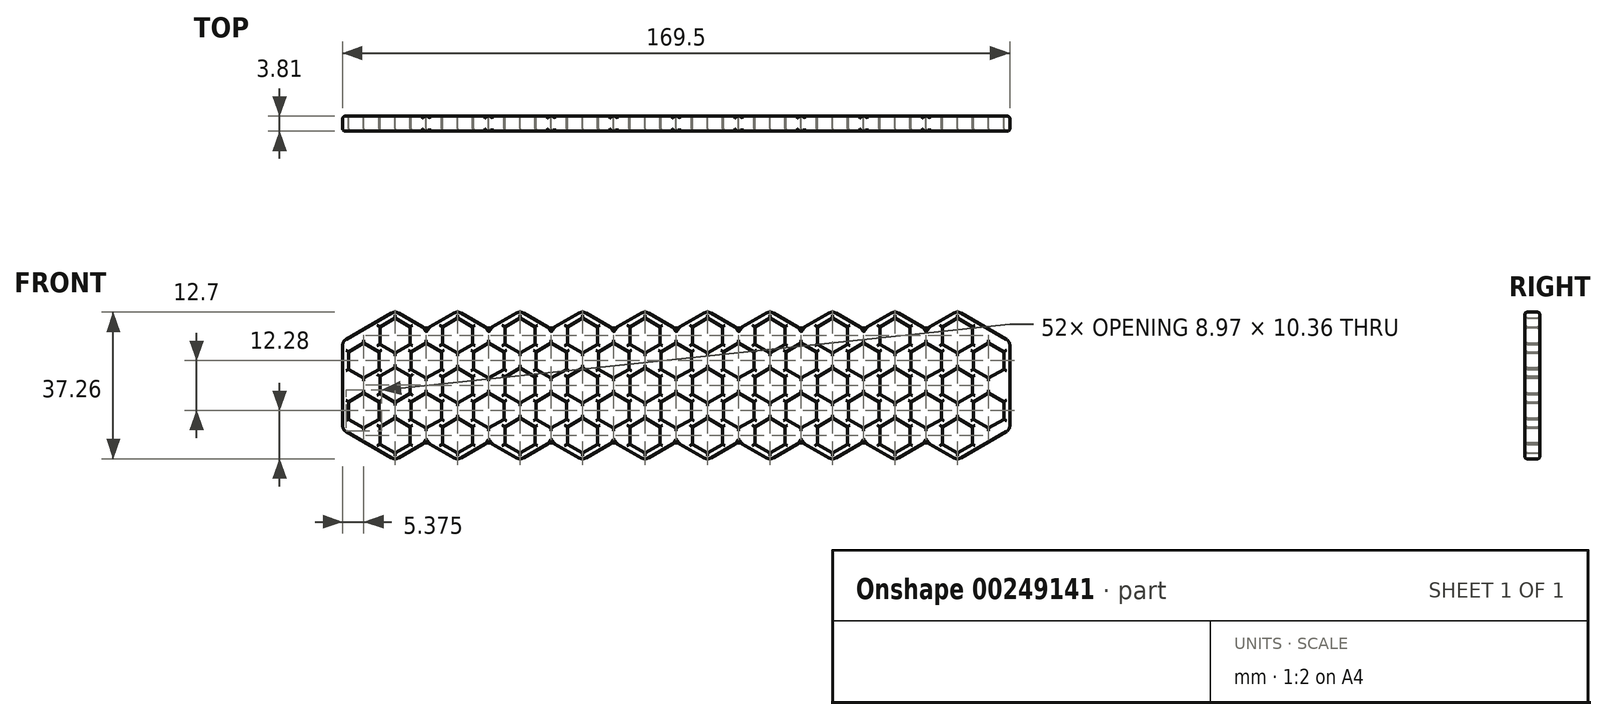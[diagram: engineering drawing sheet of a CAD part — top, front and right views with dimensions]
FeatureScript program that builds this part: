
annotation { "Feature Type Name" : "Feature", "Feature Type Description" : "" }
export const myFeature = defineFeature(function(context is Context, id is Id, definition is map)
    precondition{}
    {
        {
            var Q0;
            Q0=qCreatedBy(makeId("Front.planeOp"),FACE);
            var sketch = newSketch(context, id + "F3", { "sketchPlane" : qUnion([Q0])});
            skPoint(sketch, "E0.middle", {"position": v(0, 0) * mm});
            skPoint(sketch, "E1.cCircle.centerSnap0", {"position": v(-63.5, 0) * mm});
            skLineSegment(sketch, "E1.0", {"start": v(-63.5, 1.9) * mm, "end": v(-67.35, 4.13) * mm});
            skLineSegment(sketch, "E1.1", {"start": v(-67.35, 4.13) * mm, "end": v(-67.35, 8.57) * mm});
            skLineSegment(sketch, "E1.2", {"start": v(-67.35, 8.57) * mm, "end": v(-63.5, 10.8) * mm});
            skLineSegment(sketch, "E1.3", {"start": v(-63.5, 10.8) * mm, "end": v(-59.65, 8.57) * mm});
            skLineSegment(sketch, "E1.4", {"start": v(-59.65, 8.57) * mm, "end": v(-59.65, 4.13) * mm});
            skLineSegment(sketch, "E1.5", {"start": v(-59.65, 4.13) * mm, "end": v(-63.5, 1.9) * mm});
            skLineSegment(sketch, "E2.0", {"start": v(-71.45, -4.29) * mm, "end": v(-75.3, -2.06) * mm});
            skLineSegment(sketch, "E2.1", {"start": v(-75.3, -2.06) * mm, "end": v(-75.3, 2.38) * mm});
            skLineSegment(sketch, "E2.2", {"start": v(-75.3, 2.38) * mm, "end": v(-71.45, 4.6) * mm});
            skLineSegment(sketch, "E2.3", {"start": v(-71.45, 4.6) * mm, "end": v(-67.6, 2.38) * mm});
            skLineSegment(sketch, "E2.4", {"start": v(-67.6, 2.38) * mm, "end": v(-67.6, -2.06) * mm});
            skLineSegment(sketch, "E2.5", {"start": v(-67.6, -2.06) * mm, "end": v(-71.45, -4.29) * mm});
            skLineSegment(sketch, "E3.0", {"start": v(-63.5, -10.8) * mm, "end": v(-67.35, -8.57) * mm});
            skLineSegment(sketch, "E3.1", {"start": v(-67.35, -8.57) * mm, "end": v(-67.35, -4.13) * mm});
            skLineSegment(sketch, "E3.2", {"start": v(-67.35, -4.13) * mm, "end": v(-63.5, -1.9) * mm});
            skLineSegment(sketch, "E3.3", {"start": v(-63.5, -1.9) * mm, "end": v(-59.65, -4.13) * mm});
            skLineSegment(sketch, "E3.4", {"start": v(-59.65, -4.13) * mm, "end": v(-59.65, -8.57) * mm});
            skLineSegment(sketch, "E3.5", {"start": v(-59.65, -8.57) * mm, "end": v(-63.5, -10.8) * mm});
            skLineSegment(sketch, "E4.0", {"start": v(-47.63, 1.9) * mm, "end": v(-51.47, 4.13) * mm});
            skLineSegment(sketch, "E4.1", {"start": v(-51.47, 4.13) * mm, "end": v(-51.47, 8.57) * mm});
            skLineSegment(sketch, "E4.2", {"start": v(-51.47, 8.57) * mm, "end": v(-47.63, 10.8) * mm});
            skLineSegment(sketch, "E4.3", {"start": v(-47.63, 10.8) * mm, "end": v(-43.78, 8.57) * mm});
            skLineSegment(sketch, "E4.4", {"start": v(-43.78, 8.57) * mm, "end": v(-43.78, 4.13) * mm});
            skLineSegment(sketch, "E4.5", {"start": v(-43.78, 4.13) * mm, "end": v(-47.63, 1.9) * mm});
            skLineSegment(sketch, "E5.0", {"start": v(-47.63, -10.8) * mm, "end": v(-51.47, -8.57) * mm});
            skLineSegment(sketch, "E5.1", {"start": v(-51.47, -8.57) * mm, "end": v(-51.47, -4.13) * mm});
            skLineSegment(sketch, "E5.2", {"start": v(-51.47, -4.13) * mm, "end": v(-47.27, -1.7) * mm});
            skLineSegment(sketch, "E5.3", {"start": v(-47.63, -1.9) * mm, "end": v(-43.78, -4.13) * mm});
            skLineSegment(sketch, "E5.4", {"start": v(-43.78, -4.13) * mm, "end": v(-43.78, -8.57) * mm});
            skLineSegment(sketch, "E5.5", {"start": v(-43.78, -8.57) * mm, "end": v(-47.63, -10.8) * mm});
            skLineSegment(sketch, "E6.0", {"start": v(-31.75, 10.8) * mm, "end": v(-27.9, 8.57) * mm});
            skLineSegment(sketch, "E6.1", {"start": v(-27.9, 8.57) * mm, "end": v(-27.9, 4.13) * mm});
            skLineSegment(sketch, "E6.2", {"start": v(-27.9, 4.13) * mm, "end": v(-31.75, 1.9) * mm});
            skLineSegment(sketch, "E6.3", {"start": v(-31.75, 1.9) * mm, "end": v(-35.6, 4.13) * mm});
            skLineSegment(sketch, "E6.4", {"start": v(-35.6, 4.13) * mm, "end": v(-35.6, 8.57) * mm});
            skLineSegment(sketch, "E6.5", {"start": v(-35.6, 8.57) * mm, "end": v(-31.75, 10.8) * mm});
            skLineSegment(sketch, "E7.0", {"start": v(-31.75, -10.8) * mm, "end": v(-35.6, -8.57) * mm});
            skLineSegment(sketch, "E7.1", {"start": v(-35.6, -8.57) * mm, "end": v(-35.6, -4.13) * mm});
            skLineSegment(sketch, "E7.2", {"start": v(-35.6, -4.13) * mm, "end": v(-31.75, -1.9) * mm});
            skLineSegment(sketch, "E7.3", {"start": v(-31.75, -1.9) * mm, "end": v(-27.9, -4.13) * mm});
            skLineSegment(sketch, "E7.4", {"start": v(-27.9, -4.13) * mm, "end": v(-27.9, -8.57) * mm});
            skLineSegment(sketch, "E7.5", {"start": v(-27.9, -8.57) * mm, "end": v(-31.75, -10.8) * mm});
            skLineSegment(sketch, "E8.0", {"start": v(-15.88, 10.8) * mm, "end": v(-12.03, 8.57) * mm});
            skLineSegment(sketch, "E8.1", {"start": v(-12.03, 8.57) * mm, "end": v(-12.03, 4.13) * mm});
            skLineSegment(sketch, "E8.2", {"start": v(-12.03, 4.13) * mm, "end": v(-15.88, 1.9) * mm});
            skLineSegment(sketch, "E8.3", {"start": v(-15.88, 1.9) * mm, "end": v(-19.72, 4.13) * mm});
            skLineSegment(sketch, "E8.4", {"start": v(-19.72, 4.13) * mm, "end": v(-19.72, 8.57) * mm});
            skLineSegment(sketch, "E8.5", {"start": v(-19.72, 8.57) * mm, "end": v(-15.88, 10.8) * mm});
            skLineSegment(sketch, "E9.0", {"start": v(-15.88, -10.8) * mm, "end": v(-19.72, -8.57) * mm});
            skLineSegment(sketch, "E9.1", {"start": v(-19.72, -8.57) * mm, "end": v(-19.72, -4.13) * mm});
            skLineSegment(sketch, "E9.2", {"start": v(-19.72, -4.13) * mm, "end": v(-15.88, -1.9) * mm});
            skLineSegment(sketch, "E9.3", {"start": v(-15.88, -1.9) * mm, "end": v(-12.03, -4.13) * mm});
            skLineSegment(sketch, "E9.4", {"start": v(-12.03, -4.13) * mm, "end": v(-12.03, -8.57) * mm});
            skLineSegment(sketch, "E9.5", {"start": v(-12.03, -8.57) * mm, "end": v(-15.88, -10.8) * mm});
            skLineSegment(sketch, "E10.0", {"start": v(0, 10.8) * mm, "end": v(3.85, 8.57) * mm});
            skLineSegment(sketch, "E10.1", {"start": v(3.85, 8.57) * mm, "end": v(3.85, 4.13) * mm});
            skLineSegment(sketch, "E10.2", {"start": v(3.85, 4.13) * mm, "end": v(0, 1.9) * mm});
            skLineSegment(sketch, "E10.3", {"start": v(0, 1.9) * mm, "end": v(-3.85, 4.13) * mm});
            skLineSegment(sketch, "E10.4", {"start": v(-3.85, 4.13) * mm, "end": v(-3.85, 8.57) * mm});
            skLineSegment(sketch, "E10.5", {"start": v(-3.85, 8.57) * mm, "end": v(0, 10.8) * mm});
            skLineSegment(sketch, "E11.0", {"start": v(0, -10.8) * mm, "end": v(-3.85, -8.57) * mm});
            skLineSegment(sketch, "E11.1", {"start": v(-3.85, -8.57) * mm, "end": v(-3.85, -4.13) * mm});
            skLineSegment(sketch, "E11.2", {"start": v(-3.85, -4.13) * mm, "end": v(0, -1.9) * mm});
            skLineSegment(sketch, "E11.3", {"start": v(0, -1.9) * mm, "end": v(3.85, -4.13) * mm});
            skLineSegment(sketch, "E11.4", {"start": v(3.85, -4.13) * mm, "end": v(3.85, -8.57) * mm});
            skLineSegment(sketch, "E11.5", {"start": v(3.85, -8.57) * mm, "end": v(0, -10.8) * mm});
            skLineSegment(sketch, "E12.0", {"start": v(15.87, 10.8) * mm, "end": v(19.72, 8.57) * mm});
            skLineSegment(sketch, "E12.1", {"start": v(19.72, 8.57) * mm, "end": v(19.72, 4.13) * mm});
            skLineSegment(sketch, "E12.2", {"start": v(19.72, 4.13) * mm, "end": v(15.87, 1.9) * mm});
            skLineSegment(sketch, "E12.3", {"start": v(15.87, 1.9) * mm, "end": v(12.03, 4.13) * mm});
            skLineSegment(sketch, "E12.4", {"start": v(12.03, 4.13) * mm, "end": v(12.03, 8.57) * mm});
            skLineSegment(sketch, "E12.5", {"start": v(12.03, 8.57) * mm, "end": v(15.87, 10.8) * mm});
            skLineSegment(sketch, "E13.0", {"start": v(15.87, -10.8) * mm, "end": v(12.03, -8.57) * mm});
            skLineSegment(sketch, "E13.1", {"start": v(12.03, -8.57) * mm, "end": v(12.03, -4.13) * mm});
            skLineSegment(sketch, "E13.2", {"start": v(12.03, -4.13) * mm, "end": v(15.87, -1.9) * mm});
            skLineSegment(sketch, "E13.3", {"start": v(15.87, -1.9) * mm, "end": v(19.72, -4.13) * mm});
            skLineSegment(sketch, "E13.4", {"start": v(19.72, -4.13) * mm, "end": v(19.72, -8.57) * mm});
            skLineSegment(sketch, "E13.5", {"start": v(19.72, -8.57) * mm, "end": v(15.87, -10.8) * mm});
            skPoint(sketch, "E14.cCircle.perimeterSnap0", {"position": v(31.75, 0) * mm});
            skLineSegment(sketch, "E14.0", {"start": v(31.75, 10.8) * mm, "end": v(35.6, 8.57) * mm});
            skPoint(sketch, "E14.0.startSnap0", {"position": v(31.75, 0) * mm});
            skLineSegment(sketch, "E14.1", {"start": v(35.6, 8.57) * mm, "end": v(35.6, 4.13) * mm});
            skLineSegment(sketch, "E14.2", {"start": v(35.6, 4.13) * mm, "end": v(31.75, 1.9) * mm});
            skLineSegment(sketch, "E14.3", {"start": v(31.75, 1.9) * mm, "end": v(27.9, 4.13) * mm});
            skLineSegment(sketch, "E14.4", {"start": v(27.9, 4.13) * mm, "end": v(27.9, 8.57) * mm});
            skLineSegment(sketch, "E14.5", {"start": v(27.9, 8.57) * mm, "end": v(31.75, 10.8) * mm});
            skLineSegment(sketch, "E15.0", {"start": v(31.75, -10.8) * mm, "end": v(27.9, -8.57) * mm});
            skLineSegment(sketch, "E15.1", {"start": v(27.9, -8.57) * mm, "end": v(27.9, -4.13) * mm});
            skLineSegment(sketch, "E15.2", {"start": v(27.9, -4.13) * mm, "end": v(31.75, -1.9) * mm});
            skLineSegment(sketch, "E15.3", {"start": v(31.75, -1.9) * mm, "end": v(35.6, -4.13) * mm});
            skLineSegment(sketch, "E15.4", {"start": v(35.6, -4.13) * mm, "end": v(35.6, -8.57) * mm});
            skLineSegment(sketch, "E15.5", {"start": v(35.6, -8.57) * mm, "end": v(31.75, -10.8) * mm});
            skLineSegment(sketch, "E16.0", {"start": v(47.62, 10.8) * mm, "end": v(51.47, 8.57) * mm});
            skLineSegment(sketch, "E16.1", {"start": v(51.47, 8.57) * mm, "end": v(51.47, 4.13) * mm});
            skLineSegment(sketch, "E16.2", {"start": v(51.47, 4.13) * mm, "end": v(47.62, 1.9) * mm});
            skLineSegment(sketch, "E16.3", {"start": v(47.62, 1.9) * mm, "end": v(43.78, 4.13) * mm});
            skLineSegment(sketch, "E16.4", {"start": v(43.78, 4.13) * mm, "end": v(43.78, 8.57) * mm});
            skLineSegment(sketch, "E16.5", {"start": v(43.78, 8.57) * mm, "end": v(47.62, 10.8) * mm});
            skLineSegment(sketch, "E17.0", {"start": v(47.62, -10.8) * mm, "end": v(43.78, -8.57) * mm});
            skLineSegment(sketch, "E17.1", {"start": v(43.78, -8.57) * mm, "end": v(43.78, -4.13) * mm});
            skLineSegment(sketch, "E17.2", {"start": v(43.78, -4.13) * mm, "end": v(47.62, -1.9) * mm});
            skLineSegment(sketch, "E17.3", {"start": v(47.62, -1.9) * mm, "end": v(51.47, -4.13) * mm});
            skLineSegment(sketch, "E17.4", {"start": v(51.47, -4.13) * mm, "end": v(51.47, -8.57) * mm});
            skLineSegment(sketch, "E17.5", {"start": v(51.47, -8.57) * mm, "end": v(47.62, -10.8) * mm});
            skLineSegment(sketch, "E18.0", {"start": v(63.5, 10.8) * mm, "end": v(67.35, 8.57) * mm});
            skLineSegment(sketch, "E18.1", {"start": v(67.35, 8.57) * mm, "end": v(67.35, 4.13) * mm});
            skLineSegment(sketch, "E18.2", {"start": v(67.35, 4.13) * mm, "end": v(63.5, 1.9) * mm});
            skLineSegment(sketch, "E18.3", {"start": v(63.5, 1.9) * mm, "end": v(59.65, 4.13) * mm});
            skLineSegment(sketch, "E18.4", {"start": v(59.65, 4.13) * mm, "end": v(59.65, 8.57) * mm});
            skLineSegment(sketch, "E18.5", {"start": v(59.65, 8.57) * mm, "end": v(63.5, 10.8) * mm});
            skLineSegment(sketch, "E19.0", {"start": v(63.5, -10.8) * mm, "end": v(59.65, -8.57) * mm});
            skLineSegment(sketch, "E19.1", {"start": v(59.65, -8.57) * mm, "end": v(59.65, -4.13) * mm});
            skLineSegment(sketch, "E19.2", {"start": v(59.65, -4.13) * mm, "end": v(63.5, -1.9) * mm});
            skLineSegment(sketch, "E19.3", {"start": v(63.5, -1.9) * mm, "end": v(67.35, -4.13) * mm});
            skLineSegment(sketch, "E19.4", {"start": v(67.35, -4.13) * mm, "end": v(67.35, -8.57) * mm});
            skLineSegment(sketch, "E19.5", {"start": v(67.35, -8.57) * mm, "end": v(63.5, -10.8) * mm});
            skPoint(sketch, "E20.cCircle.centerSnap0", {"position": v(-55.58, 0.35) * mm});
            skLineSegment(sketch, "E20.0", {"start": v(-55.58, -4.44) * mm, "end": v(-59.42, -2.22) * mm});
            skLineSegment(sketch, "E20.1", {"start": v(-59.42, -2.22) * mm, "end": v(-59.42, 2.22) * mm});
            skLineSegment(sketch, "E20.2", {"start": v(-59.42, 2.22) * mm, "end": v(-55.58, 4.44) * mm});
            skLineSegment(sketch, "E20.3", {"start": v(-55.58, 4.44) * mm, "end": v(-51.73, 2.22) * mm});
            skLineSegment(sketch, "E20.4", {"start": v(-51.73, 2.22) * mm, "end": v(-51.73, -2.22) * mm});
            skLineSegment(sketch, "E20.5", {"start": v(-51.73, -2.22) * mm, "end": v(-55.58, -4.44) * mm});
            skLineSegment(sketch, "E21.0", {"start": v(-39.7, -4.44) * mm, "end": v(-43.55, -2.22) * mm});
            skLineSegment(sketch, "E21.1", {"start": v(-43.55, -2.22) * mm, "end": v(-43.55, 2.22) * mm});
            skLineSegment(sketch, "E21.2", {"start": v(-43.55, 2.22) * mm, "end": v(-39.7, 4.44) * mm});
            skLineSegment(sketch, "E21.3", {"start": v(-39.7, 4.44) * mm, "end": v(-35.85, 2.22) * mm});
            skLineSegment(sketch, "E21.4", {"start": v(-35.85, 2.22) * mm, "end": v(-35.85, -2.22) * mm});
            skLineSegment(sketch, "E21.5", {"start": v(-35.85, -2.22) * mm, "end": v(-39.7, -4.44) * mm});
            skPoint(sketch, "E22.cCircle.centerSnap0", {"position": v(-23.83, 0.35) * mm});
            skLineSegment(sketch, "E22.0", {"start": v(-23.83, 4.45) * mm, "end": v(-19.98, 2.22) * mm});
            skLineSegment(sketch, "E22.1", {"start": v(-19.98, 2.22) * mm, "end": v(-19.98, -2.22) * mm});
            skLineSegment(sketch, "E22.2", {"start": v(-19.98, -2.22) * mm, "end": v(-23.83, -4.44) * mm});
            skLineSegment(sketch, "E22.3", {"start": v(-23.83, -4.44) * mm, "end": v(-27.67, -2.22) * mm});
            skLineSegment(sketch, "E22.4", {"start": v(-27.67, -2.22) * mm, "end": v(-27.67, 2.22) * mm});
            skLineSegment(sketch, "E22.5", {"start": v(-27.67, 2.22) * mm, "end": v(-23.83, 4.45) * mm});
            skPoint(sketch, "E23.cCircle.centerSnap0", {"position": v(-7.95, 0.35) * mm});
            skLineSegment(sketch, "E23.0", {"start": v(-7.95, -4.44) * mm, "end": v(-11.8, -2.22) * mm});
            skLineSegment(sketch, "E23.1", {"start": v(-11.8, -2.22) * mm, "end": v(-11.8, 2.22) * mm});
            skLineSegment(sketch, "E23.2", {"start": v(-11.8, 2.22) * mm, "end": v(-7.95, 4.45) * mm});
            skLineSegment(sketch, "E23.3", {"start": v(-7.95, 4.45) * mm, "end": v(-4.1, 2.22) * mm});
            skLineSegment(sketch, "E23.4", {"start": v(-4.1, 2.22) * mm, "end": v(-4.1, -2.22) * mm});
            skLineSegment(sketch, "E23.5", {"start": v(-4.1, -2.22) * mm, "end": v(-7.95, -4.44) * mm});
            skPoint(sketch, "E24.cCircle.centerSnap0", {"position": v(7.92, 0.35) * mm});
            skLineSegment(sketch, "E24.0", {"start": v(7.92, -4.44) * mm, "end": v(4.08, -2.22) * mm});
            skLineSegment(sketch, "E24.1", {"start": v(4.08, -2.22) * mm, "end": v(4.08, 2.22) * mm});
            skLineSegment(sketch, "E24.2", {"start": v(4.08, 2.22) * mm, "end": v(7.92, 4.45) * mm});
            skLineSegment(sketch, "E24.3", {"start": v(7.92, 4.45) * mm, "end": v(11.77, 2.22) * mm});
            skLineSegment(sketch, "E24.4", {"start": v(11.77, 2.22) * mm, "end": v(11.77, -2.22) * mm});
            skLineSegment(sketch, "E24.5", {"start": v(11.77, -2.22) * mm, "end": v(7.92, -4.44) * mm});
            skPoint(sketch, "E25.cCircle.centerSnap0", {"position": v(23.8, 0.35) * mm});
            skLineSegment(sketch, "E25.0", {"start": v(23.8, -4.44) * mm, "end": v(19.95, -2.22) * mm});
            skLineSegment(sketch, "E25.1", {"start": v(19.95, -2.22) * mm, "end": v(19.95, 2.22) * mm});
            skLineSegment(sketch, "E25.2", {"start": v(19.95, 2.22) * mm, "end": v(23.8, 4.45) * mm});
            skLineSegment(sketch, "E25.3", {"start": v(23.8, 4.45) * mm, "end": v(27.65, 2.22) * mm});
            skLineSegment(sketch, "E25.4", {"start": v(27.65, 2.22) * mm, "end": v(27.65, -2.22) * mm});
            skLineSegment(sketch, "E25.5", {"start": v(27.65, -2.22) * mm, "end": v(23.8, -4.44) * mm});
            skLineSegment(sketch, "E26.0", {"start": v(39.67, 4.45) * mm, "end": v(43.52, 2.22) * mm});
            skLineSegment(sketch, "E26.1", {"start": v(43.52, 2.22) * mm, "end": v(43.52, -2.22) * mm});
            skLineSegment(sketch, "E26.2", {"start": v(43.52, -2.22) * mm, "end": v(39.67, -4.44) * mm});
            skLineSegment(sketch, "E26.3", {"start": v(39.67, -4.44) * mm, "end": v(35.83, -2.22) * mm});
            skLineSegment(sketch, "E26.4", {"start": v(35.83, -2.22) * mm, "end": v(35.83, 2.22) * mm});
            skLineSegment(sketch, "E26.5", {"start": v(35.83, 2.22) * mm, "end": v(39.67, 4.45) * mm});
            skLineSegment(sketch, "E27.0", {"start": v(55.55, -4.44) * mm, "end": v(51.7, -2.22) * mm});
            skLineSegment(sketch, "E27.1", {"start": v(51.7, -2.22) * mm, "end": v(51.7, 2.22) * mm});
            skLineSegment(sketch, "E27.2", {"start": v(51.7, 2.22) * mm, "end": v(55.55, 4.44) * mm});
            skLineSegment(sketch, "E27.3", {"start": v(55.55, 4.44) * mm, "end": v(59.4, 2.22) * mm});
            skLineSegment(sketch, "E27.4", {"start": v(59.4, 2.22) * mm, "end": v(59.4, -2.22) * mm});
            skLineSegment(sketch, "E27.5", {"start": v(59.4, -2.22) * mm, "end": v(55.55, -4.44) * mm});
            skLineSegment(sketch, "E28.0", {"start": v(71.42, -4.44) * mm, "end": v(67.58, -2.22) * mm});
            skLineSegment(sketch, "E28.1", {"start": v(67.58, -2.22) * mm, "end": v(67.58, 2.22) * mm});
            skLineSegment(sketch, "E28.2", {"start": v(67.58, 2.22) * mm, "end": v(71.42, 4.45) * mm});
            skLineSegment(sketch, "E28.3", {"start": v(71.42, 4.45) * mm, "end": v(75.27, 2.22) * mm});
            skLineSegment(sketch, "E28.4", {"start": v(75.27, 2.22) * mm, "end": v(75.27, -2.22) * mm});
            skLineSegment(sketch, "E28.5", {"start": v(75.27, -2.22) * mm, "end": v(71.42, -4.44) * mm});
            skLineSegment(sketch, "E29.0", {"start": v(-79.38, 1.9) * mm, "end": v(-83.22, 4.13) * mm});
            skLineSegment(sketch, "E29.1", {"start": v(-83.22, 4.13) * mm, "end": v(-83.22, 8.57) * mm});
            skLineSegment(sketch, "E29.2", {"start": v(-83.22, 8.57) * mm, "end": v(-79.38, 10.8) * mm});
            skLineSegment(sketch, "E29.3", {"start": v(-79.38, 10.8) * mm, "end": v(-75.53, 8.57) * mm});
            skLineSegment(sketch, "E29.4", {"start": v(-75.53, 8.57) * mm, "end": v(-75.53, 4.13) * mm});
            skLineSegment(sketch, "E29.5", {"start": v(-75.53, 4.13) * mm, "end": v(-79.38, 1.9) * mm});
            skLineSegment(sketch, "E30.0", {"start": v(-79.38, -10.8) * mm, "end": v(-83.22, -8.57) * mm});
            skLineSegment(sketch, "E30.1", {"start": v(-83.22, -8.57) * mm, "end": v(-83.22, -4.13) * mm});
            skLineSegment(sketch, "E30.2", {"start": v(-83.22, -4.13) * mm, "end": v(-79.38, -1.9) * mm});
            skLineSegment(sketch, "E30.3", {"start": v(-79.38, -1.9) * mm, "end": v(-75.53, -4.13) * mm});
            skLineSegment(sketch, "E30.4", {"start": v(-75.53, -4.13) * mm, "end": v(-75.53, -8.57) * mm});
            skLineSegment(sketch, "E30.5", {"start": v(-75.53, -8.57) * mm, "end": v(-79.38, -10.8) * mm});
            skPoint(sketch, "E31.orphan", {"position": v(-71.45, 13.02) * mm});
            skLineSegment(sketch, "E32.0", {"start": v(-71.45, 17.14) * mm, "end": v(-67.6, 14.92) * mm});
            skLineSegment(sketch, "E32.1", {"start": v(-67.6, 14.92) * mm, "end": v(-67.6, 10.48) * mm});
            skLineSegment(sketch, "E32.2", {"start": v(-67.6, 10.48) * mm, "end": v(-71.45, 8.26) * mm});
            skLineSegment(sketch, "E32.3", {"start": v(-71.45, 8.26) * mm, "end": v(-75.3, 10.48) * mm});
            skLineSegment(sketch, "E32.4", {"start": v(-75.3, 10.48) * mm, "end": v(-75.3, 14.92) * mm});
            skLineSegment(sketch, "E32.5", {"start": v(-75.3, 14.92) * mm, "end": v(-71.45, 17.15) * mm});
            skLineSegment(sketch, "E33.0", {"start": v(-55.58, 17.14) * mm, "end": v(-51.73, 14.92) * mm});
            skLineSegment(sketch, "E33.1", {"start": v(-51.73, 14.92) * mm, "end": v(-51.73, 10.48) * mm});
            skLineSegment(sketch, "E33.2", {"start": v(-51.73, 10.48) * mm, "end": v(-55.58, 8.26) * mm});
            skLineSegment(sketch, "E33.3", {"start": v(-55.58, 8.26) * mm, "end": v(-59.42, 10.48) * mm});
            skLineSegment(sketch, "E33.4", {"start": v(-59.42, 10.48) * mm, "end": v(-59.42, 14.92) * mm});
            skLineSegment(sketch, "E33.5", {"start": v(-59.42, 14.92) * mm, "end": v(-55.58, 17.15) * mm});
            skLineSegment(sketch, "E34.0", {"start": v(-39.7, 17.14) * mm, "end": v(-35.85, 14.92) * mm});
            skLineSegment(sketch, "E34.1", {"start": v(-35.85, 14.92) * mm, "end": v(-35.85, 10.48) * mm});
            skLineSegment(sketch, "E34.2", {"start": v(-35.85, 10.48) * mm, "end": v(-39.7, 8.26) * mm});
            skLineSegment(sketch, "E34.3", {"start": v(-39.7, 8.26) * mm, "end": v(-43.55, 10.48) * mm});
            skLineSegment(sketch, "E34.4", {"start": v(-43.55, 10.48) * mm, "end": v(-43.55, 14.92) * mm});
            skLineSegment(sketch, "E34.5", {"start": v(-43.55, 14.92) * mm, "end": v(-39.7, 17.14) * mm});
            skLineSegment(sketch, "E35.0", {"start": v(-23.83, 17.14) * mm, "end": v(-19.98, 14.92) * mm});
            skLineSegment(sketch, "E35.1", {"start": v(-19.98, 14.92) * mm, "end": v(-19.98, 10.48) * mm});
            skLineSegment(sketch, "E35.2", {"start": v(-19.98, 10.48) * mm, "end": v(-23.83, 8.26) * mm});
            skLineSegment(sketch, "E35.3", {"start": v(-23.83, 8.26) * mm, "end": v(-27.67, 10.48) * mm});
            skLineSegment(sketch, "E35.4", {"start": v(-27.67, 10.48) * mm, "end": v(-27.67, 14.92) * mm});
            skLineSegment(sketch, "E35.5", {"start": v(-27.67, 14.92) * mm, "end": v(-23.83, 17.15) * mm});
            skLineSegment(sketch, "E36.0", {"start": v(-7.95, 17.15) * mm, "end": v(-4.1, 14.92) * mm});
            skLineSegment(sketch, "E36.1", {"start": v(-4.1, 14.92) * mm, "end": v(-4.1, 10.48) * mm});
            skLineSegment(sketch, "E36.2", {"start": v(-4.1, 10.48) * mm, "end": v(-7.95, 8.26) * mm});
            skLineSegment(sketch, "E36.3", {"start": v(-7.95, 8.26) * mm, "end": v(-11.8, 10.48) * mm});
            skLineSegment(sketch, "E36.4", {"start": v(-11.8, 10.48) * mm, "end": v(-11.8, 14.92) * mm});
            skLineSegment(sketch, "E36.5", {"start": v(-11.8, 14.92) * mm, "end": v(-7.95, 17.15) * mm});
            skLineSegment(sketch, "E37.0", {"start": v(7.92, 17.15) * mm, "end": v(11.77, 14.92) * mm});
            skLineSegment(sketch, "E37.1", {"start": v(11.77, 14.92) * mm, "end": v(11.77, 10.48) * mm});
            skLineSegment(sketch, "E37.2", {"start": v(11.77, 10.48) * mm, "end": v(7.92, 8.26) * mm});
            skLineSegment(sketch, "E37.3", {"start": v(7.92, 8.26) * mm, "end": v(4.08, 10.48) * mm});
            skLineSegment(sketch, "E37.4", {"start": v(4.08, 10.48) * mm, "end": v(4.08, 14.92) * mm});
            skLineSegment(sketch, "E37.5", {"start": v(4.08, 14.92) * mm, "end": v(7.92, 17.15) * mm});
            skLineSegment(sketch, "E38.0", {"start": v(23.8, 17.15) * mm, "end": v(27.65, 14.92) * mm});
            skLineSegment(sketch, "E38.1", {"start": v(27.65, 14.92) * mm, "end": v(27.65, 10.48) * mm});
            skLineSegment(sketch, "E38.2", {"start": v(27.65, 10.48) * mm, "end": v(23.8, 8.26) * mm});
            skLineSegment(sketch, "E38.3", {"start": v(23.8, 8.26) * mm, "end": v(19.95, 10.48) * mm});
            skLineSegment(sketch, "E38.4", {"start": v(19.95, 10.48) * mm, "end": v(19.95, 14.92) * mm});
            skLineSegment(sketch, "E38.5", {"start": v(19.95, 14.92) * mm, "end": v(23.8, 17.15) * mm});
            skLineSegment(sketch, "E39.0", {"start": v(55.55, 17.15) * mm, "end": v(59.4, 14.92) * mm});
            skLineSegment(sketch, "E39.1", {"start": v(59.4, 14.92) * mm, "end": v(59.4, 10.48) * mm});
            skLineSegment(sketch, "E39.2", {"start": v(59.4, 10.48) * mm, "end": v(55.55, 8.26) * mm});
            skLineSegment(sketch, "E39.3", {"start": v(55.55, 8.26) * mm, "end": v(51.7, 10.48) * mm});
            skLineSegment(sketch, "E39.4", {"start": v(51.7, 10.48) * mm, "end": v(51.7, 14.92) * mm});
            skLineSegment(sketch, "E39.5", {"start": v(51.7, 14.92) * mm, "end": v(55.55, 17.15) * mm});
            skLineSegment(sketch, "E40.0", {"start": v(71.42, 17.15) * mm, "end": v(75.27, 14.92) * mm});
            skLineSegment(sketch, "E40.1", {"start": v(75.27, 14.92) * mm, "end": v(75.27, 10.48) * mm});
            skLineSegment(sketch, "E40.2", {"start": v(75.27, 10.48) * mm, "end": v(71.42, 8.25) * mm});
            skLineSegment(sketch, "E40.3", {"start": v(71.42, 8.25) * mm, "end": v(67.58, 10.48) * mm});
            skLineSegment(sketch, "E40.4", {"start": v(67.58, 10.48) * mm, "end": v(67.58, 14.92) * mm});
            skLineSegment(sketch, "E40.5", {"start": v(67.58, 14.92) * mm, "end": v(71.42, 17.15) * mm});
            skLineSegment(sketch, "E41.0", {"start": v(39.67, 17.15) * mm, "end": v(43.52, 14.92) * mm});
            skLineSegment(sketch, "E41.1", {"start": v(43.52, 14.92) * mm, "end": v(43.52, 10.48) * mm});
            skLineSegment(sketch, "E41.2", {"start": v(43.52, 10.48) * mm, "end": v(39.67, 8.26) * mm});
            skLineSegment(sketch, "E41.3", {"start": v(39.67, 8.26) * mm, "end": v(35.83, 10.48) * mm});
            skLineSegment(sketch, "E41.4", {"start": v(35.83, 10.48) * mm, "end": v(35.83, 14.92) * mm});
            skLineSegment(sketch, "E41.5", {"start": v(35.83, 14.92) * mm, "end": v(39.67, 17.15) * mm});
            skPoint(sketch, "E42.orphan", {"position": v(-55.58, -12) * mm});
            skPoint(sketch, "E43.orphan", {"position": v(-23.83, -12) * mm});
            skPoint(sketch, "E44.orphan", {"position": v(-7.95, -12) * mm});
            skPoint(sketch, "E45.orphan", {"position": v(7.92, -12) * mm});
            skPoint(sketch, "E46.orphan", {"position": v(23.8, -12) * mm});
            skLineSegment(sketch, "E47.0", {"start": v(-71.45, -17.14) * mm, "end": v(-75.3, -14.92) * mm});
            skLineSegment(sketch, "E47.1", {"start": v(-75.3, -14.92) * mm, "end": v(-75.3, -10.48) * mm});
            skLineSegment(sketch, "E47.2", {"start": v(-75.3, -10.48) * mm, "end": v(-71.45, -8.26) * mm});
            skLineSegment(sketch, "E47.3", {"start": v(-71.45, -8.26) * mm, "end": v(-67.6, -10.48) * mm});
            skLineSegment(sketch, "E47.4", {"start": v(-67.6, -10.48) * mm, "end": v(-67.6, -14.92) * mm});
            skLineSegment(sketch, "E47.5", {"start": v(-67.6, -14.92) * mm, "end": v(-71.45, -17.14) * mm});
            skLineSegment(sketch, "E48.0", {"start": v(-55.58, -17.14) * mm, "end": v(-59.42, -14.92) * mm});
            skLineSegment(sketch, "E48.1", {"start": v(-59.42, -14.92) * mm, "end": v(-59.42, -10.48) * mm});
            skLineSegment(sketch, "E48.2", {"start": v(-59.42, -10.48) * mm, "end": v(-55.58, -8.26) * mm});
            skLineSegment(sketch, "E48.3", {"start": v(-55.58, -8.26) * mm, "end": v(-51.73, -10.48) * mm});
            skLineSegment(sketch, "E48.4", {"start": v(-51.73, -10.48) * mm, "end": v(-51.73, -14.92) * mm});
            skLineSegment(sketch, "E48.5", {"start": v(-51.73, -14.92) * mm, "end": v(-55.58, -17.14) * mm});
            skLineSegment(sketch, "E49.0", {"start": v(-39.7, -17.14) * mm, "end": v(-43.55, -14.92) * mm});
            skLineSegment(sketch, "E49.1", {"start": v(-43.55, -14.92) * mm, "end": v(-43.55, -10.48) * mm});
            skLineSegment(sketch, "E49.2", {"start": v(-43.55, -10.48) * mm, "end": v(-39.7, -8.26) * mm});
            skLineSegment(sketch, "E49.3", {"start": v(-39.7, -8.26) * mm, "end": v(-35.85, -10.48) * mm});
            skLineSegment(sketch, "E49.4", {"start": v(-35.85, -10.48) * mm, "end": v(-35.85, -14.92) * mm});
            skLineSegment(sketch, "E49.5", {"start": v(-35.85, -14.92) * mm, "end": v(-39.7, -17.14) * mm});
            skLineSegment(sketch, "E50.0", {"start": v(-23.83, -17.14) * mm, "end": v(-27.67, -14.92) * mm});
            skLineSegment(sketch, "E50.1", {"start": v(-27.67, -14.92) * mm, "end": v(-27.67, -10.48) * mm});
            skLineSegment(sketch, "E50.2", {"start": v(-27.67, -10.48) * mm, "end": v(-23.83, -8.26) * mm});
            skLineSegment(sketch, "E50.3", {"start": v(-23.83, -8.26) * mm, "end": v(-19.98, -10.48) * mm});
            skLineSegment(sketch, "E50.4", {"start": v(-19.98, -10.48) * mm, "end": v(-19.98, -14.92) * mm});
            skLineSegment(sketch, "E50.5", {"start": v(-19.98, -14.92) * mm, "end": v(-23.83, -17.14) * mm});
            skLineSegment(sketch, "E51.0", {"start": v(-7.95, -17.14) * mm, "end": v(-11.8, -14.92) * mm});
            skLineSegment(sketch, "E51.1", {"start": v(-11.8, -14.92) * mm, "end": v(-11.8, -10.48) * mm});
            skLineSegment(sketch, "E51.2", {"start": v(-11.8, -10.48) * mm, "end": v(-7.95, -8.26) * mm});
            skLineSegment(sketch, "E51.3", {"start": v(-7.95, -8.26) * mm, "end": v(-4.1, -10.48) * mm});
            skLineSegment(sketch, "E51.4", {"start": v(-4.1, -10.48) * mm, "end": v(-4.1, -14.92) * mm});
            skLineSegment(sketch, "E51.5", {"start": v(-4.1, -14.92) * mm, "end": v(-7.95, -17.14) * mm});
            skLineSegment(sketch, "E52.0", {"start": v(7.92, -17.14) * mm, "end": v(4.08, -14.92) * mm});
            skLineSegment(sketch, "E52.1", {"start": v(4.08, -14.92) * mm, "end": v(4.08, -10.48) * mm});
            skLineSegment(sketch, "E52.2", {"start": v(4.08, -10.48) * mm, "end": v(7.92, -8.26) * mm});
            skLineSegment(sketch, "E52.3", {"start": v(7.92, -8.26) * mm, "end": v(11.77, -10.48) * mm});
            skLineSegment(sketch, "E52.4", {"start": v(11.77, -10.48) * mm, "end": v(11.77, -14.92) * mm});
            skLineSegment(sketch, "E52.5", {"start": v(11.77, -14.92) * mm, "end": v(7.92, -17.14) * mm});
            skLineSegment(sketch, "E53.0", {"start": v(23.8, -17.14) * mm, "end": v(19.95, -14.92) * mm});
            skLineSegment(sketch, "E53.1", {"start": v(19.95, -14.92) * mm, "end": v(19.95, -10.48) * mm});
            skLineSegment(sketch, "E53.2", {"start": v(19.95, -10.48) * mm, "end": v(23.8, -8.26) * mm});
            skLineSegment(sketch, "E53.3", {"start": v(23.8, -8.26) * mm, "end": v(27.65, -10.48) * mm});
            skLineSegment(sketch, "E53.4", {"start": v(27.65, -10.48) * mm, "end": v(27.65, -14.92) * mm});
            skLineSegment(sketch, "E53.5", {"start": v(27.65, -14.92) * mm, "end": v(23.8, -17.14) * mm});
            skLineSegment(sketch, "E54.0", {"start": v(39.67, -17.14) * mm, "end": v(35.83, -14.92) * mm});
            skLineSegment(sketch, "E54.1", {"start": v(35.83, -14.92) * mm, "end": v(35.83, -10.48) * mm});
            skLineSegment(sketch, "E54.2", {"start": v(35.83, -10.48) * mm, "end": v(39.67, -8.26) * mm});
            skLineSegment(sketch, "E54.3", {"start": v(39.67, -8.26) * mm, "end": v(43.52, -10.48) * mm});
            skLineSegment(sketch, "E54.4", {"start": v(43.52, -10.48) * mm, "end": v(43.52, -14.92) * mm});
            skLineSegment(sketch, "E54.5", {"start": v(43.52, -14.92) * mm, "end": v(39.67, -17.14) * mm});
            skLineSegment(sketch, "E55.0", {"start": v(55.55, -17.14) * mm, "end": v(51.7, -14.92) * mm});
            skLineSegment(sketch, "E55.1", {"start": v(51.7, -14.92) * mm, "end": v(51.7, -10.48) * mm});
            skLineSegment(sketch, "E55.2", {"start": v(51.7, -10.48) * mm, "end": v(55.55, -8.26) * mm});
            skLineSegment(sketch, "E55.3", {"start": v(55.55, -8.26) * mm, "end": v(59.4, -10.48) * mm});
            skLineSegment(sketch, "E55.4", {"start": v(59.4, -10.48) * mm, "end": v(59.4, -14.92) * mm});
            skLineSegment(sketch, "E55.5", {"start": v(59.4, -14.92) * mm, "end": v(55.55, -17.14) * mm});
            skLineSegment(sketch, "E56.0", {"start": v(71.42, -17.14) * mm, "end": v(67.58, -14.92) * mm});
            skLineSegment(sketch, "E56.1", {"start": v(67.58, -14.92) * mm, "end": v(67.58, -10.48) * mm});
            skLineSegment(sketch, "E56.2", {"start": v(67.58, -10.48) * mm, "end": v(71.42, -8.25) * mm});
            skLineSegment(sketch, "E56.3", {"start": v(71.42, -8.26) * mm, "end": v(75.27, -10.48) * mm});
            skLineSegment(sketch, "E56.4", {"start": v(75.27, -10.48) * mm, "end": v(75.27, -14.92) * mm});
            skLineSegment(sketch, "E56.5", {"start": v(75.27, -14.92) * mm, "end": v(71.42, -17.14) * mm});
            skLineSegment(sketch, "E57.0", {"start": v(79.38, -10.8) * mm, "end": v(75.53, -8.57) * mm});
            skLineSegment(sketch, "E57.1", {"start": v(75.53, -8.57) * mm, "end": v(75.53, -4.13) * mm});
            skLineSegment(sketch, "E57.2", {"start": v(75.53, -4.13) * mm, "end": v(79.38, -1.9) * mm});
            skLineSegment(sketch, "E57.3", {"start": v(79.38, -1.9) * mm, "end": v(83.22, -4.13) * mm});
            skLineSegment(sketch, "E57.4", {"start": v(83.22, -4.13) * mm, "end": v(83.22, -8.57) * mm});
            skLineSegment(sketch, "E57.5", {"start": v(83.22, -8.57) * mm, "end": v(79.38, -10.8) * mm});
            skLineSegment(sketch, "E58.0", {"start": v(79.38, 1.9) * mm, "end": v(75.53, 4.13) * mm});
            skLineSegment(sketch, "E58.1", {"start": v(75.53, 4.13) * mm, "end": v(75.53, 8.57) * mm});
            skLineSegment(sketch, "E58.2", {"start": v(75.53, 8.57) * mm, "end": v(79.38, 10.8) * mm});
            skLineSegment(sketch, "E58.3", {"start": v(79.38, 10.8) * mm, "end": v(83.22, 8.57) * mm});
            skLineSegment(sketch, "E58.4", {"start": v(83.22, 8.57) * mm, "end": v(83.22, 4.13) * mm});
            skLineSegment(sketch, "E58.5", {"start": v(83.22, 4.13) * mm, "end": v(79.38, 1.9) * mm});
            skLineSegment(sketch, "E59.0", {"start": v(-84.75, -11.23) * mm, "end": v(-84.75, 11.23) * mm});
            skLineSegment(sketch, "E60.0", {"start": v(-84.75, 11.23) * mm, "end": v(-71.45, 18.9) * mm});
            skLineSegment(sketch, "E61.trimOffspring", {"start": v(-75, 10.03) * mm, "end": v(-74.76, 9.9) * mm});
            skLineSegment(sketch, "E62.0", {"start": v(-55.58, 18.9) * mm, "end": v(-47.64, 14.32) * mm});
            skLineSegment(sketch, "E63.0", {"start": v(-47.64, 14.32) * mm, "end": v(-39.7, 18.9) * mm});
            skLineSegment(sketch, "E64.0", {"start": v(-39.7, 18.9) * mm, "end": v(-31.76, 14.32) * mm});
            skLineSegment(sketch, "E65.0", {"start": v(-31.76, 14.32) * mm, "end": v(-23.83, 18.9) * mm});
            skLineSegment(sketch, "E66.0", {"start": v(-71.45, 18.9) * mm, "end": v(-63.51, 14.32) * mm});
            skLineSegment(sketch, "E67.0", {"start": v(-63.51, 14.32) * mm, "end": v(-55.58, 18.9) * mm});
            skLineSegment(sketch, "E68.0", {"start": v(-23.83, 18.9) * mm, "end": v(-15.89, 14.32) * mm});
            skLineSegment(sketch, "E69.0", {"start": v(-15.89, 14.32) * mm, "end": v(-7.95, 18.9) * mm});
            skLineSegment(sketch, "E70.0", {"start": v(-7.95, 18.9) * mm, "end": v(-0.01, 14.32) * mm});
            skLineSegment(sketch, "E71.0", {"start": v(-0.01, 14.32) * mm, "end": v(7.92, 18.9) * mm});
            skLineSegment(sketch, "E72.0", {"start": v(7.92, 18.9) * mm, "end": v(15.86, 14.32) * mm});
            skLineSegment(sketch, "E73.0", {"start": v(15.86, 14.32) * mm, "end": v(23.8, 18.9) * mm});
            skLineSegment(sketch, "E74.0", {"start": v(23.8, 18.9) * mm, "end": v(31.74, 14.32) * mm});
            skLineSegment(sketch, "E75.0", {"start": v(31.74, 14.32) * mm, "end": v(39.67, 18.9) * mm});
            skLineSegment(sketch, "E76.0", {"start": v(39.67, 18.9) * mm, "end": v(47.61, 14.32) * mm});
            skLineSegment(sketch, "E77.0", {"start": v(47.61, 14.32) * mm, "end": v(55.55, 18.9) * mm});
            skLineSegment(sketch, "E78.0", {"start": v(63.49, 14.32) * mm, "end": v(71.42, 18.9) * mm});
            skLineSegment(sketch, "E79.0", {"start": v(55.55, 18.9) * mm, "end": v(63.49, 14.32) * mm});
            skLineSegment(sketch, "E80.0", {"start": v(71.42, 18.9) * mm, "end": v(84.75, 11.21) * mm});
            skLineSegment(sketch, "E81.0", {"start": v(84.75, 11.21) * mm, "end": v(84.75, -11.21) * mm});
            skLineSegment(sketch, "E82.0", {"start": v(84.75, -11.21) * mm, "end": v(71.42, -18.9) * mm});
            skLineSegment(sketch, "E83.0", {"start": v(71.42, -18.9) * mm, "end": v(63.49, -14.32) * mm});
            skLineSegment(sketch, "E84.0", {"start": v(63.49, -14.32) * mm, "end": v(55.55, -18.9) * mm});
            skLineSegment(sketch, "E85.0", {"start": v(55.55, -18.9) * mm, "end": v(47.61, -14.32) * mm});
            skLineSegment(sketch, "E86.0", {"start": v(47.61, -14.32) * mm, "end": v(39.67, -18.9) * mm});
            skLineSegment(sketch, "E87.0", {"start": v(39.67, -18.9) * mm, "end": v(31.74, -14.32) * mm});
            skLineSegment(sketch, "E88.0", {"start": v(31.74, -14.32) * mm, "end": v(23.8, -18.9) * mm});
            skLineSegment(sketch, "E89.0", {"start": v(23.8, -18.9) * mm, "end": v(15.86, -14.32) * mm});
            skLineSegment(sketch, "E90.0", {"start": v(15.86, -14.32) * mm, "end": v(7.92, -18.9) * mm});
            skLineSegment(sketch, "E91.0", {"start": v(7.92, -18.9) * mm, "end": v(-0.01, -14.32) * mm});
            skLineSegment(sketch, "E92.0", {"start": v(-0.01, -14.32) * mm, "end": v(-7.95, -18.9) * mm});
            skLineSegment(sketch, "E93.0", {"start": v(-7.95, -18.9) * mm, "end": v(-15.89, -14.32) * mm});
            skLineSegment(sketch, "E94.0", {"start": v(-15.89, -14.32) * mm, "end": v(-23.83, -18.9) * mm});
            skLineSegment(sketch, "E95.0", {"start": v(-23.83, -18.9) * mm, "end": v(-31.76, -14.32) * mm});
            skLineSegment(sketch, "E96.0", {"start": v(-31.76, -14.32) * mm, "end": v(-39.7, -18.9) * mm});
            skLineSegment(sketch, "E97.0", {"start": v(-39.7, -18.9) * mm, "end": v(-47.64, -14.32) * mm});
            skLineSegment(sketch, "E98.0", {"start": v(-47.64, -14.32) * mm, "end": v(-55.58, -18.9) * mm});
            skLineSegment(sketch, "E99.0", {"start": v(-55.58, -18.9) * mm, "end": v(-63.51, -14.32) * mm});
            skLineSegment(sketch, "E100.0", {"start": v(-63.51, -14.32) * mm, "end": v(-71.45, -18.9) * mm});
            skLineSegment(sketch, "E101.0", {"start": v(-71.45, -18.9) * mm, "end": v(-84.75, -11.23) * mm});
            skSolve(sketch);
        }
        {
            var Q0;
            Q0=makeQuery(id+"F3.imprint","IMPRINT",FACE,{"disambiguationData":[TD([[makeQuery(id+"F3.imprint","IMPRINT",EDGE,{"derivedFrom":sQuery(id+"F3.wireOp",EDGE,"E1.0")}),1.0]])]});
            extrude(context, id + "F0", {"entities" : qUnion([Q0]), "depth" : 3.8 * mm});
        }
        {
            var Q0;
            Q0=makeQuery(id+"F0.opExtrude","CAP_FACE",FACE,{"disambiguationData":[OSD([sQuery(id+"F3.wireOp",EDGE,"E1.0"),sQuery(id+"F3.wireOp",EDGE,"E1.1"),sQuery(id+"F3.wireOp",EDGE,"E1.2"),sQuery(id+"F3.wireOp",EDGE,"E1.3"),sQuery(id+"F3.wireOp",EDGE,"E1.4"),sQuery(id+"F3.wireOp",EDGE,"E1.5"),sQuery(id+"F3.wireOp",EDGE,"E2.0"),sQuery(id+"F3.wireOp",EDGE,"E2.1"),sQuery(id+"F3.wireOp",EDGE,"E2.2"),sQuery(id+"F3.wireOp",EDGE,"E2.3"),sQuery(id+"F3.wireOp",EDGE,"E2.4"),sQuery(id+"F3.wireOp",EDGE,"E2.5"),sQuery(id+"F3.wireOp",EDGE,"E3.0"),sQuery(id+"F3.wireOp",EDGE,"E3.1"),sQuery(id+"F3.wireOp",EDGE,"E3.2"),sQuery(id+"F3.wireOp",EDGE,"E3.3"),sQuery(id+"F3.wireOp",EDGE,"E3.4"),sQuery(id+"F3.wireOp",EDGE,"E3.5"),sQuery(id+"F3.wireOp",EDGE,"E4.0"),sQuery(id+"F3.wireOp",EDGE,"E4.1"),sQuery(id+"F3.wireOp",EDGE,"E4.2"),sQuery(id+"F3.wireOp",EDGE,"E4.3"),sQuery(id+"F3.wireOp",EDGE,"E4.4"),sQuery(id+"F3.wireOp",EDGE,"E4.5"),sQuery(id+"F3.wireOp",EDGE,"E5.0"),sQuery(id+"F3.wireOp",EDGE,"E5.1"),sQuery(id+"F3.wireOp",EDGE,"E5.2"),sQuery(id+"F3.wireOp",EDGE,"E5.3"),sQuery(id+"F3.wireOp",EDGE,"E5.4"),sQuery(id+"F3.wireOp",EDGE,"E5.5"),sQuery(id+"F3.wireOp",EDGE,"E6.0"),sQuery(id+"F3.wireOp",EDGE,"E6.1"),sQuery(id+"F3.wireOp",EDGE,"E6.2"),sQuery(id+"F3.wireOp",EDGE,"E6.3"),sQuery(id+"F3.wireOp",EDGE,"E6.4"),sQuery(id+"F3.wireOp",EDGE,"E6.5"),sQuery(id+"F3.wireOp",EDGE,"E7.0"),sQuery(id+"F3.wireOp",EDGE,"E7.1"),sQuery(id+"F3.wireOp",EDGE,"E7.2"),sQuery(id+"F3.wireOp",EDGE,"E7.3"),sQuery(id+"F3.wireOp",EDGE,"E7.4"),sQuery(id+"F3.wireOp",EDGE,"E7.5"),sQuery(id+"F3.wireOp",EDGE,"E8.0"),sQuery(id+"F3.wireOp",EDGE,"E8.1"),sQuery(id+"F3.wireOp",EDGE,"E8.2"),sQuery(id+"F3.wireOp",EDGE,"E8.3"),sQuery(id+"F3.wireOp",EDGE,"E8.4"),sQuery(id+"F3.wireOp",EDGE,"E8.5"),sQuery(id+"F3.wireOp",EDGE,"E9.0"),sQuery(id+"F3.wireOp",EDGE,"E9.1"),sQuery(id+"F3.wireOp",EDGE,"E9.2"),sQuery(id+"F3.wireOp",EDGE,"E9.3"),sQuery(id+"F3.wireOp",EDGE,"E9.4"),sQuery(id+"F3.wireOp",EDGE,"E9.5"),sQuery(id+"F3.wireOp",EDGE,"E10.0"),sQuery(id+"F3.wireOp",EDGE,"E10.1"),sQuery(id+"F3.wireOp",EDGE,"E10.2"),sQuery(id+"F3.wireOp",EDGE,"E10.3"),sQuery(id+"F3.wireOp",EDGE,"E10.4"),sQuery(id+"F3.wireOp",EDGE,"E10.5"),sQuery(id+"F3.wireOp",EDGE,"E11.0"),sQuery(id+"F3.wireOp",EDGE,"E11.1"),sQuery(id+"F3.wireOp",EDGE,"E11.2"),sQuery(id+"F3.wireOp",EDGE,"E11.3"),sQuery(id+"F3.wireOp",EDGE,"E11.4"),sQuery(id+"F3.wireOp",EDGE,"E11.5"),sQuery(id+"F3.wireOp",EDGE,"E12.0"),sQuery(id+"F3.wireOp",EDGE,"E12.1"),sQuery(id+"F3.wireOp",EDGE,"E12.2"),sQuery(id+"F3.wireOp",EDGE,"E12.3"),sQuery(id+"F3.wireOp",EDGE,"E12.4"),sQuery(id+"F3.wireOp",EDGE,"E12.5"),sQuery(id+"F3.wireOp",EDGE,"E13.0"),sQuery(id+"F3.wireOp",EDGE,"E13.1"),sQuery(id+"F3.wireOp",EDGE,"E13.2"),sQuery(id+"F3.wireOp",EDGE,"E13.3"),sQuery(id+"F3.wireOp",EDGE,"E13.4"),sQuery(id+"F3.wireOp",EDGE,"E13.5"),sQuery(id+"F3.wireOp",EDGE,"E14.0"),sQuery(id+"F3.wireOp",EDGE,"E14.1"),sQuery(id+"F3.wireOp",EDGE,"E14.2"),sQuery(id+"F3.wireOp",EDGE,"E14.3"),sQuery(id+"F3.wireOp",EDGE,"E14.4"),sQuery(id+"F3.wireOp",EDGE,"E14.5"),sQuery(id+"F3.wireOp",EDGE,"E15.0"),sQuery(id+"F3.wireOp",EDGE,"E15.1"),sQuery(id+"F3.wireOp",EDGE,"E15.2"),sQuery(id+"F3.wireOp",EDGE,"E15.3"),sQuery(id+"F3.wireOp",EDGE,"E15.4"),sQuery(id+"F3.wireOp",EDGE,"E15.5"),sQuery(id+"F3.wireOp",EDGE,"E16.0"),sQuery(id+"F3.wireOp",EDGE,"E16.1"),sQuery(id+"F3.wireOp",EDGE,"E16.2"),sQuery(id+"F3.wireOp",EDGE,"E16.3"),sQuery(id+"F3.wireOp",EDGE,"E16.4"),sQuery(id+"F3.wireOp",EDGE,"E16.5"),sQuery(id+"F3.wireOp",EDGE,"E17.0"),sQuery(id+"F3.wireOp",EDGE,"E17.1"),sQuery(id+"F3.wireOp",EDGE,"E17.2"),sQuery(id+"F3.wireOp",EDGE,"E17.3"),sQuery(id+"F3.wireOp",EDGE,"E17.4"),sQuery(id+"F3.wireOp",EDGE,"E17.5"),sQuery(id+"F3.wireOp",EDGE,"E18.0"),sQuery(id+"F3.wireOp",EDGE,"E18.1"),sQuery(id+"F3.wireOp",EDGE,"E18.2"),sQuery(id+"F3.wireOp",EDGE,"E18.3"),sQuery(id+"F3.wireOp",EDGE,"E18.4"),sQuery(id+"F3.wireOp",EDGE,"E18.5"),sQuery(id+"F3.wireOp",EDGE,"E19.0"),sQuery(id+"F3.wireOp",EDGE,"E19.1"),sQuery(id+"F3.wireOp",EDGE,"E19.2"),sQuery(id+"F3.wireOp",EDGE,"E19.3"),sQuery(id+"F3.wireOp",EDGE,"E19.4"),sQuery(id+"F3.wireOp",EDGE,"E19.5"),sQuery(id+"F3.wireOp",EDGE,"E20.0"),sQuery(id+"F3.wireOp",EDGE,"E20.1"),sQuery(id+"F3.wireOp",EDGE,"E20.2"),sQuery(id+"F3.wireOp",EDGE,"E20.3"),sQuery(id+"F3.wireOp",EDGE,"E20.4"),sQuery(id+"F3.wireOp",EDGE,"E20.5"),sQuery(id+"F3.wireOp",EDGE,"E21.0"),sQuery(id+"F3.wireOp",EDGE,"E21.1"),sQuery(id+"F3.wireOp",EDGE,"E21.2"),sQuery(id+"F3.wireOp",EDGE,"E21.3"),sQuery(id+"F3.wireOp",EDGE,"E21.4"),sQuery(id+"F3.wireOp",EDGE,"E21.5"),sQuery(id+"F3.wireOp",EDGE,"E22.0"),sQuery(id+"F3.wireOp",EDGE,"E22.1"),sQuery(id+"F3.wireOp",EDGE,"E22.2"),sQuery(id+"F3.wireOp",EDGE,"E22.3"),sQuery(id+"F3.wireOp",EDGE,"E22.4"),sQuery(id+"F3.wireOp",EDGE,"E22.5"),sQuery(id+"F3.wireOp",EDGE,"E23.0"),sQuery(id+"F3.wireOp",EDGE,"E23.1"),sQuery(id+"F3.wireOp",EDGE,"E23.2"),sQuery(id+"F3.wireOp",EDGE,"E23.3"),sQuery(id+"F3.wireOp",EDGE,"E23.4"),sQuery(id+"F3.wireOp",EDGE,"E23.5"),sQuery(id+"F3.wireOp",EDGE,"E24.0"),sQuery(id+"F3.wireOp",EDGE,"E24.1"),sQuery(id+"F3.wireOp",EDGE,"E24.2"),sQuery(id+"F3.wireOp",EDGE,"E24.3"),sQuery(id+"F3.wireOp",EDGE,"E24.4"),sQuery(id+"F3.wireOp",EDGE,"E24.5"),sQuery(id+"F3.wireOp",EDGE,"E25.0"),sQuery(id+"F3.wireOp",EDGE,"E25.1"),sQuery(id+"F3.wireOp",EDGE,"E25.2"),sQuery(id+"F3.wireOp",EDGE,"E25.3"),sQuery(id+"F3.wireOp",EDGE,"E25.4"),sQuery(id+"F3.wireOp",EDGE,"E25.5"),sQuery(id+"F3.wireOp",EDGE,"E26.0"),sQuery(id+"F3.wireOp",EDGE,"E26.1"),sQuery(id+"F3.wireOp",EDGE,"E26.2"),sQuery(id+"F3.wireOp",EDGE,"E26.3"),sQuery(id+"F3.wireOp",EDGE,"E26.4"),sQuery(id+"F3.wireOp",EDGE,"E26.5"),sQuery(id+"F3.wireOp",EDGE,"E27.0"),sQuery(id+"F3.wireOp",EDGE,"E27.1"),sQuery(id+"F3.wireOp",EDGE,"E27.2"),sQuery(id+"F3.wireOp",EDGE,"E27.3"),sQuery(id+"F3.wireOp",EDGE,"E27.4"),sQuery(id+"F3.wireOp",EDGE,"E27.5"),sQuery(id+"F3.wireOp",EDGE,"E28.0"),sQuery(id+"F3.wireOp",EDGE,"E28.1"),sQuery(id+"F3.wireOp",EDGE,"E28.2"),sQuery(id+"F3.wireOp",EDGE,"E28.3"),sQuery(id+"F3.wireOp",EDGE,"E28.4"),sQuery(id+"F3.wireOp",EDGE,"E28.5"),sQuery(id+"F3.wireOp",EDGE,"E29.0"),sQuery(id+"F3.wireOp",EDGE,"E29.1"),sQuery(id+"F3.wireOp",EDGE,"E29.2"),sQuery(id+"F3.wireOp",EDGE,"E29.3"),sQuery(id+"F3.wireOp",EDGE,"E29.4"),sQuery(id+"F3.wireOp",EDGE,"E29.5"),sQuery(id+"F3.wireOp",EDGE,"E30.0"),sQuery(id+"F3.wireOp",EDGE,"E30.1"),sQuery(id+"F3.wireOp",EDGE,"E30.2"),sQuery(id+"F3.wireOp",EDGE,"E30.3"),sQuery(id+"F3.wireOp",EDGE,"E30.4"),sQuery(id+"F3.wireOp",EDGE,"E30.5"),sQuery(id+"F3.wireOp",EDGE,"E32.0"),sQuery(id+"F3.wireOp",EDGE,"E32.1"),sQuery(id+"F3.wireOp",EDGE,"E32.2"),sQuery(id+"F3.wireOp",EDGE,"E32.3"),sQuery(id+"F3.wireOp",EDGE,"E32.4"),sQuery(id+"F3.wireOp",EDGE,"E32.5"),sQuery(id+"F3.wireOp",EDGE,"E33.0"),sQuery(id+"F3.wireOp",EDGE,"E33.1"),sQuery(id+"F3.wireOp",EDGE,"E33.2"),sQuery(id+"F3.wireOp",EDGE,"E33.3"),sQuery(id+"F3.wireOp",EDGE,"E33.4"),sQuery(id+"F3.wireOp",EDGE,"E33.5"),sQuery(id+"F3.wireOp",EDGE,"E34.0"),sQuery(id+"F3.wireOp",EDGE,"E34.1"),sQuery(id+"F3.wireOp",EDGE,"E34.2"),sQuery(id+"F3.wireOp",EDGE,"E34.3"),sQuery(id+"F3.wireOp",EDGE,"E34.4"),sQuery(id+"F3.wireOp",EDGE,"E34.5"),sQuery(id+"F3.wireOp",EDGE,"E35.0"),sQuery(id+"F3.wireOp",EDGE,"E35.1"),sQuery(id+"F3.wireOp",EDGE,"E35.2"),sQuery(id+"F3.wireOp",EDGE,"E35.3"),sQuery(id+"F3.wireOp",EDGE,"E35.4"),sQuery(id+"F3.wireOp",EDGE,"E35.5"),sQuery(id+"F3.wireOp",EDGE,"E36.0"),sQuery(id+"F3.wireOp",EDGE,"E36.1"),sQuery(id+"F3.wireOp",EDGE,"E36.2"),sQuery(id+"F3.wireOp",EDGE,"E36.3"),sQuery(id+"F3.wireOp",EDGE,"E36.4"),sQuery(id+"F3.wireOp",EDGE,"E36.5"),sQuery(id+"F3.wireOp",EDGE,"E37.0"),sQuery(id+"F3.wireOp",EDGE,"E37.1"),sQuery(id+"F3.wireOp",EDGE,"E37.2"),sQuery(id+"F3.wireOp",EDGE,"E37.3"),sQuery(id+"F3.wireOp",EDGE,"E37.4"),sQuery(id+"F3.wireOp",EDGE,"E37.5"),sQuery(id+"F3.wireOp",EDGE,"E38.0"),sQuery(id+"F3.wireOp",EDGE,"E38.1"),sQuery(id+"F3.wireOp",EDGE,"E38.2"),sQuery(id+"F3.wireOp",EDGE,"E38.3"),sQuery(id+"F3.wireOp",EDGE,"E38.4"),sQuery(id+"F3.wireOp",EDGE,"E38.5"),sQuery(id+"F3.wireOp",EDGE,"E39.0"),sQuery(id+"F3.wireOp",EDGE,"E39.1"),sQuery(id+"F3.wireOp",EDGE,"E39.2"),sQuery(id+"F3.wireOp",EDGE,"E39.3"),sQuery(id+"F3.wireOp",EDGE,"E39.4"),sQuery(id+"F3.wireOp",EDGE,"E39.5"),sQuery(id+"F3.wireOp",EDGE,"E40.0"),sQuery(id+"F3.wireOp",EDGE,"E40.1"),sQuery(id+"F3.wireOp",EDGE,"E40.2"),sQuery(id+"F3.wireOp",EDGE,"E40.3"),sQuery(id+"F3.wireOp",EDGE,"E40.4"),sQuery(id+"F3.wireOp",EDGE,"E40.5"),sQuery(id+"F3.wireOp",EDGE,"E41.0"),sQuery(id+"F3.wireOp",EDGE,"E41.1"),sQuery(id+"F3.wireOp",EDGE,"E41.2"),sQuery(id+"F3.wireOp",EDGE,"E41.3"),sQuery(id+"F3.wireOp",EDGE,"E41.4"),sQuery(id+"F3.wireOp",EDGE,"E41.5"),sQuery(id+"F3.wireOp",EDGE,"E47.0"),sQuery(id+"F3.wireOp",EDGE,"E47.1"),sQuery(id+"F3.wireOp",EDGE,"E47.2"),sQuery(id+"F3.wireOp",EDGE,"E47.3"),sQuery(id+"F3.wireOp",EDGE,"E47.4"),sQuery(id+"F3.wireOp",EDGE,"E47.5"),sQuery(id+"F3.wireOp",EDGE,"E48.0"),sQuery(id+"F3.wireOp",EDGE,"E48.1"),sQuery(id+"F3.wireOp",EDGE,"E48.2"),sQuery(id+"F3.wireOp",EDGE,"E48.3"),sQuery(id+"F3.wireOp",EDGE,"E48.4"),sQuery(id+"F3.wireOp",EDGE,"E48.5"),sQuery(id+"F3.wireOp",EDGE,"E49.0"),sQuery(id+"F3.wireOp",EDGE,"E49.1"),sQuery(id+"F3.wireOp",EDGE,"E49.2"),sQuery(id+"F3.wireOp",EDGE,"E49.3"),sQuery(id+"F3.wireOp",EDGE,"E49.4"),sQuery(id+"F3.wireOp",EDGE,"E49.5"),sQuery(id+"F3.wireOp",EDGE,"E50.0"),sQuery(id+"F3.wireOp",EDGE,"E50.1"),sQuery(id+"F3.wireOp",EDGE,"E50.2"),sQuery(id+"F3.wireOp",EDGE,"E50.3"),sQuery(id+"F3.wireOp",EDGE,"E50.4"),sQuery(id+"F3.wireOp",EDGE,"E50.5"),sQuery(id+"F3.wireOp",EDGE,"E51.0"),sQuery(id+"F3.wireOp",EDGE,"E51.1"),sQuery(id+"F3.wireOp",EDGE,"E51.2"),sQuery(id+"F3.wireOp",EDGE,"E51.3"),sQuery(id+"F3.wireOp",EDGE,"E51.4"),sQuery(id+"F3.wireOp",EDGE,"E51.5"),sQuery(id+"F3.wireOp",EDGE,"E52.0"),sQuery(id+"F3.wireOp",EDGE,"E52.1"),sQuery(id+"F3.wireOp",EDGE,"E52.2"),sQuery(id+"F3.wireOp",EDGE,"E52.3"),sQuery(id+"F3.wireOp",EDGE,"E52.4"),sQuery(id+"F3.wireOp",EDGE,"E52.5"),sQuery(id+"F3.wireOp",EDGE,"E53.0"),sQuery(id+"F3.wireOp",EDGE,"E53.1"),sQuery(id+"F3.wireOp",EDGE,"E53.2"),sQuery(id+"F3.wireOp",EDGE,"E53.3"),sQuery(id+"F3.wireOp",EDGE,"E53.4"),sQuery(id+"F3.wireOp",EDGE,"E53.5"),sQuery(id+"F3.wireOp",EDGE,"E54.0"),sQuery(id+"F3.wireOp",EDGE,"E54.1"),sQuery(id+"F3.wireOp",EDGE,"E54.2"),sQuery(id+"F3.wireOp",EDGE,"E54.3"),sQuery(id+"F3.wireOp",EDGE,"E54.4"),sQuery(id+"F3.wireOp",EDGE,"E54.5"),sQuery(id+"F3.wireOp",EDGE,"E55.0"),sQuery(id+"F3.wireOp",EDGE,"E55.1"),sQuery(id+"F3.wireOp",EDGE,"E55.2"),sQuery(id+"F3.wireOp",EDGE,"E55.3"),sQuery(id+"F3.wireOp",EDGE,"E55.4"),sQuery(id+"F3.wireOp",EDGE,"E55.5"),sQuery(id+"F3.wireOp",EDGE,"E56.0"),sQuery(id+"F3.wireOp",EDGE,"E56.1"),sQuery(id+"F3.wireOp",EDGE,"E56.2"),sQuery(id+"F3.wireOp",EDGE,"E56.3"),sQuery(id+"F3.wireOp",EDGE,"E56.4"),sQuery(id+"F3.wireOp",EDGE,"E56.5"),sQuery(id+"F3.wireOp",EDGE,"E57.0"),sQuery(id+"F3.wireOp",EDGE,"E57.1"),sQuery(id+"F3.wireOp",EDGE,"E57.2"),sQuery(id+"F3.wireOp",EDGE,"E57.3"),sQuery(id+"F3.wireOp",EDGE,"E57.4"),sQuery(id+"F3.wireOp",EDGE,"E57.5"),sQuery(id+"F3.wireOp",EDGE,"E58.0"),sQuery(id+"F3.wireOp",EDGE,"E58.1"),sQuery(id+"F3.wireOp",EDGE,"E58.2"),sQuery(id+"F3.wireOp",EDGE,"E58.3"),sQuery(id+"F3.wireOp",EDGE,"E58.4"),sQuery(id+"F3.wireOp",EDGE,"E58.5"),sQuery(id+"F3.wireOp",EDGE,"E59.0"),sQuery(id+"F3.wireOp",EDGE,"E60.0"),sQuery(id+"F3.wireOp",EDGE,"E62.0"),sQuery(id+"F3.wireOp",EDGE,"E63.0"),sQuery(id+"F3.wireOp",EDGE,"E64.0"),sQuery(id+"F3.wireOp",EDGE,"E65.0"),sQuery(id+"F3.wireOp",EDGE,"E66.0"),sQuery(id+"F3.wireOp",EDGE,"E67.0"),sQuery(id+"F3.wireOp",EDGE,"E68.0"),sQuery(id+"F3.wireOp",EDGE,"E69.0"),sQuery(id+"F3.wireOp",EDGE,"E70.0"),sQuery(id+"F3.wireOp",EDGE,"E71.0"),sQuery(id+"F3.wireOp",EDGE,"E72.0"),sQuery(id+"F3.wireOp",EDGE,"E73.0"),sQuery(id+"F3.wireOp",EDGE,"E74.0"),sQuery(id+"F3.wireOp",EDGE,"E75.0"),sQuery(id+"F3.wireOp",EDGE,"E76.0"),sQuery(id+"F3.wireOp",EDGE,"E77.0"),sQuery(id+"F3.wireOp",EDGE,"E78.0"),sQuery(id+"F3.wireOp",EDGE,"E79.0"),sQuery(id+"F3.wireOp",EDGE,"E80.0"),sQuery(id+"F3.wireOp",EDGE,"E81.0"),sQuery(id+"F3.wireOp",EDGE,"E82.0"),sQuery(id+"F3.wireOp",EDGE,"E83.0"),sQuery(id+"F3.wireOp",EDGE,"E84.0"),sQuery(id+"F3.wireOp",EDGE,"E85.0"),sQuery(id+"F3.wireOp",EDGE,"E86.0"),sQuery(id+"F3.wireOp",EDGE,"E87.0"),sQuery(id+"F3.wireOp",EDGE,"E88.0"),sQuery(id+"F3.wireOp",EDGE,"E89.0"),sQuery(id+"F3.wireOp",EDGE,"E90.0"),sQuery(id+"F3.wireOp",EDGE,"E91.0"),sQuery(id+"F3.wireOp",EDGE,"E92.0"),sQuery(id+"F3.wireOp",EDGE,"E93.0"),sQuery(id+"F3.wireOp",EDGE,"E94.0"),sQuery(id+"F3.wireOp",EDGE,"E95.0"),sQuery(id+"F3.wireOp",EDGE,"E96.0"),sQuery(id+"F3.wireOp",EDGE,"E97.0"),sQuery(id+"F3.wireOp",EDGE,"E98.0"),sQuery(id+"F3.wireOp",EDGE,"E99.0"),sQuery(id+"F3.wireOp",EDGE,"E100.0"),sQuery(id+"F3.wireOp",EDGE,"E101.0")])],"isStart":false});
            fillet(context, id + "F1", {"entities" : qUnion([Q0]), "radius" : 0.64 * mm, "tangentPropagation" : true, "allowEdgeOverflow" : false});
        }
        {
            var Q0;
            Q0=makeQuery(id+"F0.opExtrude","CAP_FACE",FACE,{"disambiguationData":[OSD([sQuery(id+"F3.wireOp",EDGE,"E1.0"),sQuery(id+"F3.wireOp",EDGE,"E1.1"),sQuery(id+"F3.wireOp",EDGE,"E1.2"),sQuery(id+"F3.wireOp",EDGE,"E1.3"),sQuery(id+"F3.wireOp",EDGE,"E1.4"),sQuery(id+"F3.wireOp",EDGE,"E1.5"),sQuery(id+"F3.wireOp",EDGE,"E2.0"),sQuery(id+"F3.wireOp",EDGE,"E2.1"),sQuery(id+"F3.wireOp",EDGE,"E2.2"),sQuery(id+"F3.wireOp",EDGE,"E2.3"),sQuery(id+"F3.wireOp",EDGE,"E2.4"),sQuery(id+"F3.wireOp",EDGE,"E2.5"),sQuery(id+"F3.wireOp",EDGE,"E3.0"),sQuery(id+"F3.wireOp",EDGE,"E3.1"),sQuery(id+"F3.wireOp",EDGE,"E3.2"),sQuery(id+"F3.wireOp",EDGE,"E3.3"),sQuery(id+"F3.wireOp",EDGE,"E3.4"),sQuery(id+"F3.wireOp",EDGE,"E3.5"),sQuery(id+"F3.wireOp",EDGE,"E4.0"),sQuery(id+"F3.wireOp",EDGE,"E4.1"),sQuery(id+"F3.wireOp",EDGE,"E4.2"),sQuery(id+"F3.wireOp",EDGE,"E4.3"),sQuery(id+"F3.wireOp",EDGE,"E4.4"),sQuery(id+"F3.wireOp",EDGE,"E4.5"),sQuery(id+"F3.wireOp",EDGE,"E5.0"),sQuery(id+"F3.wireOp",EDGE,"E5.1"),sQuery(id+"F3.wireOp",EDGE,"E5.2"),sQuery(id+"F3.wireOp",EDGE,"E5.3"),sQuery(id+"F3.wireOp",EDGE,"E5.4"),sQuery(id+"F3.wireOp",EDGE,"E5.5"),sQuery(id+"F3.wireOp",EDGE,"E6.0"),sQuery(id+"F3.wireOp",EDGE,"E6.1"),sQuery(id+"F3.wireOp",EDGE,"E6.2"),sQuery(id+"F3.wireOp",EDGE,"E6.3"),sQuery(id+"F3.wireOp",EDGE,"E6.4"),sQuery(id+"F3.wireOp",EDGE,"E6.5"),sQuery(id+"F3.wireOp",EDGE,"E7.0"),sQuery(id+"F3.wireOp",EDGE,"E7.1"),sQuery(id+"F3.wireOp",EDGE,"E7.2"),sQuery(id+"F3.wireOp",EDGE,"E7.3"),sQuery(id+"F3.wireOp",EDGE,"E7.4"),sQuery(id+"F3.wireOp",EDGE,"E7.5"),sQuery(id+"F3.wireOp",EDGE,"E8.0"),sQuery(id+"F3.wireOp",EDGE,"E8.1"),sQuery(id+"F3.wireOp",EDGE,"E8.2"),sQuery(id+"F3.wireOp",EDGE,"E8.3"),sQuery(id+"F3.wireOp",EDGE,"E8.4"),sQuery(id+"F3.wireOp",EDGE,"E8.5"),sQuery(id+"F3.wireOp",EDGE,"E9.0"),sQuery(id+"F3.wireOp",EDGE,"E9.1"),sQuery(id+"F3.wireOp",EDGE,"E9.2"),sQuery(id+"F3.wireOp",EDGE,"E9.3"),sQuery(id+"F3.wireOp",EDGE,"E9.4"),sQuery(id+"F3.wireOp",EDGE,"E9.5"),sQuery(id+"F3.wireOp",EDGE,"E10.0"),sQuery(id+"F3.wireOp",EDGE,"E10.1"),sQuery(id+"F3.wireOp",EDGE,"E10.2"),sQuery(id+"F3.wireOp",EDGE,"E10.3"),sQuery(id+"F3.wireOp",EDGE,"E10.4"),sQuery(id+"F3.wireOp",EDGE,"E10.5"),sQuery(id+"F3.wireOp",EDGE,"E11.0"),sQuery(id+"F3.wireOp",EDGE,"E11.1"),sQuery(id+"F3.wireOp",EDGE,"E11.2"),sQuery(id+"F3.wireOp",EDGE,"E11.3"),sQuery(id+"F3.wireOp",EDGE,"E11.4"),sQuery(id+"F3.wireOp",EDGE,"E11.5"),sQuery(id+"F3.wireOp",EDGE,"E12.0"),sQuery(id+"F3.wireOp",EDGE,"E12.1"),sQuery(id+"F3.wireOp",EDGE,"E12.2"),sQuery(id+"F3.wireOp",EDGE,"E12.3"),sQuery(id+"F3.wireOp",EDGE,"E12.4"),sQuery(id+"F3.wireOp",EDGE,"E12.5"),sQuery(id+"F3.wireOp",EDGE,"E13.0"),sQuery(id+"F3.wireOp",EDGE,"E13.1"),sQuery(id+"F3.wireOp",EDGE,"E13.2"),sQuery(id+"F3.wireOp",EDGE,"E13.3"),sQuery(id+"F3.wireOp",EDGE,"E13.4"),sQuery(id+"F3.wireOp",EDGE,"E13.5"),sQuery(id+"F3.wireOp",EDGE,"E14.0"),sQuery(id+"F3.wireOp",EDGE,"E14.1"),sQuery(id+"F3.wireOp",EDGE,"E14.2"),sQuery(id+"F3.wireOp",EDGE,"E14.3"),sQuery(id+"F3.wireOp",EDGE,"E14.4"),sQuery(id+"F3.wireOp",EDGE,"E14.5"),sQuery(id+"F3.wireOp",EDGE,"E15.0"),sQuery(id+"F3.wireOp",EDGE,"E15.1"),sQuery(id+"F3.wireOp",EDGE,"E15.2"),sQuery(id+"F3.wireOp",EDGE,"E15.3"),sQuery(id+"F3.wireOp",EDGE,"E15.4"),sQuery(id+"F3.wireOp",EDGE,"E15.5"),sQuery(id+"F3.wireOp",EDGE,"E16.0"),sQuery(id+"F3.wireOp",EDGE,"E16.1"),sQuery(id+"F3.wireOp",EDGE,"E16.2"),sQuery(id+"F3.wireOp",EDGE,"E16.3"),sQuery(id+"F3.wireOp",EDGE,"E16.4"),sQuery(id+"F3.wireOp",EDGE,"E16.5"),sQuery(id+"F3.wireOp",EDGE,"E17.0"),sQuery(id+"F3.wireOp",EDGE,"E17.1"),sQuery(id+"F3.wireOp",EDGE,"E17.2"),sQuery(id+"F3.wireOp",EDGE,"E17.3"),sQuery(id+"F3.wireOp",EDGE,"E17.4"),sQuery(id+"F3.wireOp",EDGE,"E17.5"),sQuery(id+"F3.wireOp",EDGE,"E18.0"),sQuery(id+"F3.wireOp",EDGE,"E18.1"),sQuery(id+"F3.wireOp",EDGE,"E18.2"),sQuery(id+"F3.wireOp",EDGE,"E18.3"),sQuery(id+"F3.wireOp",EDGE,"E18.4"),sQuery(id+"F3.wireOp",EDGE,"E18.5"),sQuery(id+"F3.wireOp",EDGE,"E19.0"),sQuery(id+"F3.wireOp",EDGE,"E19.1"),sQuery(id+"F3.wireOp",EDGE,"E19.2"),sQuery(id+"F3.wireOp",EDGE,"E19.3"),sQuery(id+"F3.wireOp",EDGE,"E19.4"),sQuery(id+"F3.wireOp",EDGE,"E19.5"),sQuery(id+"F3.wireOp",EDGE,"E20.0"),sQuery(id+"F3.wireOp",EDGE,"E20.1"),sQuery(id+"F3.wireOp",EDGE,"E20.2"),sQuery(id+"F3.wireOp",EDGE,"E20.3"),sQuery(id+"F3.wireOp",EDGE,"E20.4"),sQuery(id+"F3.wireOp",EDGE,"E20.5"),sQuery(id+"F3.wireOp",EDGE,"E21.0"),sQuery(id+"F3.wireOp",EDGE,"E21.1"),sQuery(id+"F3.wireOp",EDGE,"E21.2"),sQuery(id+"F3.wireOp",EDGE,"E21.3"),sQuery(id+"F3.wireOp",EDGE,"E21.4"),sQuery(id+"F3.wireOp",EDGE,"E21.5"),sQuery(id+"F3.wireOp",EDGE,"E22.0"),sQuery(id+"F3.wireOp",EDGE,"E22.1"),sQuery(id+"F3.wireOp",EDGE,"E22.2"),sQuery(id+"F3.wireOp",EDGE,"E22.3"),sQuery(id+"F3.wireOp",EDGE,"E22.4"),sQuery(id+"F3.wireOp",EDGE,"E22.5"),sQuery(id+"F3.wireOp",EDGE,"E23.0"),sQuery(id+"F3.wireOp",EDGE,"E23.1"),sQuery(id+"F3.wireOp",EDGE,"E23.2"),sQuery(id+"F3.wireOp",EDGE,"E23.3"),sQuery(id+"F3.wireOp",EDGE,"E23.4"),sQuery(id+"F3.wireOp",EDGE,"E23.5"),sQuery(id+"F3.wireOp",EDGE,"E24.0"),sQuery(id+"F3.wireOp",EDGE,"E24.1"),sQuery(id+"F3.wireOp",EDGE,"E24.2"),sQuery(id+"F3.wireOp",EDGE,"E24.3"),sQuery(id+"F3.wireOp",EDGE,"E24.4"),sQuery(id+"F3.wireOp",EDGE,"E24.5"),sQuery(id+"F3.wireOp",EDGE,"E25.0"),sQuery(id+"F3.wireOp",EDGE,"E25.1"),sQuery(id+"F3.wireOp",EDGE,"E25.2"),sQuery(id+"F3.wireOp",EDGE,"E25.3"),sQuery(id+"F3.wireOp",EDGE,"E25.4"),sQuery(id+"F3.wireOp",EDGE,"E25.5"),sQuery(id+"F3.wireOp",EDGE,"E26.0"),sQuery(id+"F3.wireOp",EDGE,"E26.1"),sQuery(id+"F3.wireOp",EDGE,"E26.2"),sQuery(id+"F3.wireOp",EDGE,"E26.3"),sQuery(id+"F3.wireOp",EDGE,"E26.4"),sQuery(id+"F3.wireOp",EDGE,"E26.5"),sQuery(id+"F3.wireOp",EDGE,"E27.0"),sQuery(id+"F3.wireOp",EDGE,"E27.1"),sQuery(id+"F3.wireOp",EDGE,"E27.2"),sQuery(id+"F3.wireOp",EDGE,"E27.3"),sQuery(id+"F3.wireOp",EDGE,"E27.4"),sQuery(id+"F3.wireOp",EDGE,"E27.5"),sQuery(id+"F3.wireOp",EDGE,"E28.0"),sQuery(id+"F3.wireOp",EDGE,"E28.1"),sQuery(id+"F3.wireOp",EDGE,"E28.2"),sQuery(id+"F3.wireOp",EDGE,"E28.3"),sQuery(id+"F3.wireOp",EDGE,"E28.4"),sQuery(id+"F3.wireOp",EDGE,"E28.5"),sQuery(id+"F3.wireOp",EDGE,"E29.0"),sQuery(id+"F3.wireOp",EDGE,"E29.1"),sQuery(id+"F3.wireOp",EDGE,"E29.2"),sQuery(id+"F3.wireOp",EDGE,"E29.3"),sQuery(id+"F3.wireOp",EDGE,"E29.4"),sQuery(id+"F3.wireOp",EDGE,"E29.5"),sQuery(id+"F3.wireOp",EDGE,"E30.0"),sQuery(id+"F3.wireOp",EDGE,"E30.1"),sQuery(id+"F3.wireOp",EDGE,"E30.2"),sQuery(id+"F3.wireOp",EDGE,"E30.3"),sQuery(id+"F3.wireOp",EDGE,"E30.4"),sQuery(id+"F3.wireOp",EDGE,"E30.5"),sQuery(id+"F3.wireOp",EDGE,"E32.0"),sQuery(id+"F3.wireOp",EDGE,"E32.1"),sQuery(id+"F3.wireOp",EDGE,"E32.2"),sQuery(id+"F3.wireOp",EDGE,"E32.3"),sQuery(id+"F3.wireOp",EDGE,"E32.4"),sQuery(id+"F3.wireOp",EDGE,"E32.5"),sQuery(id+"F3.wireOp",EDGE,"E33.0"),sQuery(id+"F3.wireOp",EDGE,"E33.1"),sQuery(id+"F3.wireOp",EDGE,"E33.2"),sQuery(id+"F3.wireOp",EDGE,"E33.3"),sQuery(id+"F3.wireOp",EDGE,"E33.4"),sQuery(id+"F3.wireOp",EDGE,"E33.5"),sQuery(id+"F3.wireOp",EDGE,"E34.0"),sQuery(id+"F3.wireOp",EDGE,"E34.1"),sQuery(id+"F3.wireOp",EDGE,"E34.2"),sQuery(id+"F3.wireOp",EDGE,"E34.3"),sQuery(id+"F3.wireOp",EDGE,"E34.4"),sQuery(id+"F3.wireOp",EDGE,"E34.5"),sQuery(id+"F3.wireOp",EDGE,"E35.0"),sQuery(id+"F3.wireOp",EDGE,"E35.1"),sQuery(id+"F3.wireOp",EDGE,"E35.2"),sQuery(id+"F3.wireOp",EDGE,"E35.3"),sQuery(id+"F3.wireOp",EDGE,"E35.4"),sQuery(id+"F3.wireOp",EDGE,"E35.5"),sQuery(id+"F3.wireOp",EDGE,"E36.0"),sQuery(id+"F3.wireOp",EDGE,"E36.1"),sQuery(id+"F3.wireOp",EDGE,"E36.2"),sQuery(id+"F3.wireOp",EDGE,"E36.3"),sQuery(id+"F3.wireOp",EDGE,"E36.4"),sQuery(id+"F3.wireOp",EDGE,"E36.5"),sQuery(id+"F3.wireOp",EDGE,"E37.0"),sQuery(id+"F3.wireOp",EDGE,"E37.1"),sQuery(id+"F3.wireOp",EDGE,"E37.2"),sQuery(id+"F3.wireOp",EDGE,"E37.3"),sQuery(id+"F3.wireOp",EDGE,"E37.4"),sQuery(id+"F3.wireOp",EDGE,"E37.5"),sQuery(id+"F3.wireOp",EDGE,"E38.0"),sQuery(id+"F3.wireOp",EDGE,"E38.1"),sQuery(id+"F3.wireOp",EDGE,"E38.2"),sQuery(id+"F3.wireOp",EDGE,"E38.3"),sQuery(id+"F3.wireOp",EDGE,"E38.4"),sQuery(id+"F3.wireOp",EDGE,"E38.5"),sQuery(id+"F3.wireOp",EDGE,"E39.0"),sQuery(id+"F3.wireOp",EDGE,"E39.1"),sQuery(id+"F3.wireOp",EDGE,"E39.2"),sQuery(id+"F3.wireOp",EDGE,"E39.3"),sQuery(id+"F3.wireOp",EDGE,"E39.4"),sQuery(id+"F3.wireOp",EDGE,"E39.5"),sQuery(id+"F3.wireOp",EDGE,"E40.0"),sQuery(id+"F3.wireOp",EDGE,"E40.1"),sQuery(id+"F3.wireOp",EDGE,"E40.2"),sQuery(id+"F3.wireOp",EDGE,"E40.3"),sQuery(id+"F3.wireOp",EDGE,"E40.4"),sQuery(id+"F3.wireOp",EDGE,"E40.5"),sQuery(id+"F3.wireOp",EDGE,"E41.0"),sQuery(id+"F3.wireOp",EDGE,"E41.1"),sQuery(id+"F3.wireOp",EDGE,"E41.2"),sQuery(id+"F3.wireOp",EDGE,"E41.3"),sQuery(id+"F3.wireOp",EDGE,"E41.4"),sQuery(id+"F3.wireOp",EDGE,"E41.5"),sQuery(id+"F3.wireOp",EDGE,"E47.0"),sQuery(id+"F3.wireOp",EDGE,"E47.1"),sQuery(id+"F3.wireOp",EDGE,"E47.2"),sQuery(id+"F3.wireOp",EDGE,"E47.3"),sQuery(id+"F3.wireOp",EDGE,"E47.4"),sQuery(id+"F3.wireOp",EDGE,"E47.5"),sQuery(id+"F3.wireOp",EDGE,"E48.0"),sQuery(id+"F3.wireOp",EDGE,"E48.1"),sQuery(id+"F3.wireOp",EDGE,"E48.2"),sQuery(id+"F3.wireOp",EDGE,"E48.3"),sQuery(id+"F3.wireOp",EDGE,"E48.4"),sQuery(id+"F3.wireOp",EDGE,"E48.5"),sQuery(id+"F3.wireOp",EDGE,"E49.0"),sQuery(id+"F3.wireOp",EDGE,"E49.1"),sQuery(id+"F3.wireOp",EDGE,"E49.2"),sQuery(id+"F3.wireOp",EDGE,"E49.3"),sQuery(id+"F3.wireOp",EDGE,"E49.4"),sQuery(id+"F3.wireOp",EDGE,"E49.5"),sQuery(id+"F3.wireOp",EDGE,"E50.0"),sQuery(id+"F3.wireOp",EDGE,"E50.1"),sQuery(id+"F3.wireOp",EDGE,"E50.2"),sQuery(id+"F3.wireOp",EDGE,"E50.3"),sQuery(id+"F3.wireOp",EDGE,"E50.4"),sQuery(id+"F3.wireOp",EDGE,"E50.5"),sQuery(id+"F3.wireOp",EDGE,"E51.0"),sQuery(id+"F3.wireOp",EDGE,"E51.1"),sQuery(id+"F3.wireOp",EDGE,"E51.2"),sQuery(id+"F3.wireOp",EDGE,"E51.3"),sQuery(id+"F3.wireOp",EDGE,"E51.4"),sQuery(id+"F3.wireOp",EDGE,"E51.5"),sQuery(id+"F3.wireOp",EDGE,"E52.0"),sQuery(id+"F3.wireOp",EDGE,"E52.1"),sQuery(id+"F3.wireOp",EDGE,"E52.2"),sQuery(id+"F3.wireOp",EDGE,"E52.3"),sQuery(id+"F3.wireOp",EDGE,"E52.4"),sQuery(id+"F3.wireOp",EDGE,"E52.5"),sQuery(id+"F3.wireOp",EDGE,"E53.0"),sQuery(id+"F3.wireOp",EDGE,"E53.1"),sQuery(id+"F3.wireOp",EDGE,"E53.2"),sQuery(id+"F3.wireOp",EDGE,"E53.3"),sQuery(id+"F3.wireOp",EDGE,"E53.4"),sQuery(id+"F3.wireOp",EDGE,"E53.5"),sQuery(id+"F3.wireOp",EDGE,"E54.0"),sQuery(id+"F3.wireOp",EDGE,"E54.1"),sQuery(id+"F3.wireOp",EDGE,"E54.2"),sQuery(id+"F3.wireOp",EDGE,"E54.3"),sQuery(id+"F3.wireOp",EDGE,"E54.4"),sQuery(id+"F3.wireOp",EDGE,"E54.5"),sQuery(id+"F3.wireOp",EDGE,"E55.0"),sQuery(id+"F3.wireOp",EDGE,"E55.1"),sQuery(id+"F3.wireOp",EDGE,"E55.2"),sQuery(id+"F3.wireOp",EDGE,"E55.3"),sQuery(id+"F3.wireOp",EDGE,"E55.4"),sQuery(id+"F3.wireOp",EDGE,"E55.5"),sQuery(id+"F3.wireOp",EDGE,"E56.0"),sQuery(id+"F3.wireOp",EDGE,"E56.1"),sQuery(id+"F3.wireOp",EDGE,"E56.2"),sQuery(id+"F3.wireOp",EDGE,"E56.3"),sQuery(id+"F3.wireOp",EDGE,"E56.4"),sQuery(id+"F3.wireOp",EDGE,"E56.5"),sQuery(id+"F3.wireOp",EDGE,"E57.0"),sQuery(id+"F3.wireOp",EDGE,"E57.1"),sQuery(id+"F3.wireOp",EDGE,"E57.2"),sQuery(id+"F3.wireOp",EDGE,"E57.3"),sQuery(id+"F3.wireOp",EDGE,"E57.4"),sQuery(id+"F3.wireOp",EDGE,"E57.5"),sQuery(id+"F3.wireOp",EDGE,"E58.0"),sQuery(id+"F3.wireOp",EDGE,"E58.1"),sQuery(id+"F3.wireOp",EDGE,"E58.2"),sQuery(id+"F3.wireOp",EDGE,"E58.3"),sQuery(id+"F3.wireOp",EDGE,"E58.4"),sQuery(id+"F3.wireOp",EDGE,"E58.5"),sQuery(id+"F3.wireOp",EDGE,"E59.0"),sQuery(id+"F3.wireOp",EDGE,"E60.0"),sQuery(id+"F3.wireOp",EDGE,"E62.0"),sQuery(id+"F3.wireOp",EDGE,"E63.0"),sQuery(id+"F3.wireOp",EDGE,"E64.0"),sQuery(id+"F3.wireOp",EDGE,"E65.0"),sQuery(id+"F3.wireOp",EDGE,"E66.0"),sQuery(id+"F3.wireOp",EDGE,"E67.0"),sQuery(id+"F3.wireOp",EDGE,"E68.0"),sQuery(id+"F3.wireOp",EDGE,"E69.0"),sQuery(id+"F3.wireOp",EDGE,"E70.0"),sQuery(id+"F3.wireOp",EDGE,"E71.0"),sQuery(id+"F3.wireOp",EDGE,"E72.0"),sQuery(id+"F3.wireOp",EDGE,"E73.0"),sQuery(id+"F3.wireOp",EDGE,"E74.0"),sQuery(id+"F3.wireOp",EDGE,"E75.0"),sQuery(id+"F3.wireOp",EDGE,"E76.0"),sQuery(id+"F3.wireOp",EDGE,"E77.0"),sQuery(id+"F3.wireOp",EDGE,"E78.0"),sQuery(id+"F3.wireOp",EDGE,"E79.0"),sQuery(id+"F3.wireOp",EDGE,"E80.0"),sQuery(id+"F3.wireOp",EDGE,"E81.0"),sQuery(id+"F3.wireOp",EDGE,"E82.0"),sQuery(id+"F3.wireOp",EDGE,"E83.0"),sQuery(id+"F3.wireOp",EDGE,"E84.0"),sQuery(id+"F3.wireOp",EDGE,"E85.0"),sQuery(id+"F3.wireOp",EDGE,"E86.0"),sQuery(id+"F3.wireOp",EDGE,"E87.0"),sQuery(id+"F3.wireOp",EDGE,"E88.0"),sQuery(id+"F3.wireOp",EDGE,"E89.0"),sQuery(id+"F3.wireOp",EDGE,"E90.0"),sQuery(id+"F3.wireOp",EDGE,"E91.0"),sQuery(id+"F3.wireOp",EDGE,"E92.0"),sQuery(id+"F3.wireOp",EDGE,"E93.0"),sQuery(id+"F3.wireOp",EDGE,"E94.0"),sQuery(id+"F3.wireOp",EDGE,"E95.0"),sQuery(id+"F3.wireOp",EDGE,"E96.0"),sQuery(id+"F3.wireOp",EDGE,"E97.0"),sQuery(id+"F3.wireOp",EDGE,"E98.0"),sQuery(id+"F3.wireOp",EDGE,"E99.0"),sQuery(id+"F3.wireOp",EDGE,"E100.0"),sQuery(id+"F3.wireOp",EDGE,"E101.0")])],"isStart":true});
            fillet(context, id + "F4", {"entities" : qUnion([Q0]), "radius" : 0.64 * mm, "tangentPropagation" : true, "allowEdgeOverflow" : false});
        }
        {
            var Q0;
            Q0=makeQuery(id+"F0.opExtrude","SWEPT_EDGE",EDGE,{"disambiguationData":[OSD([sQuery(id+"F3.wireOp",EDGE,"E100.0"),sQuery(id+"F3.wireOp",EDGE,"E101.0")])]});
            var Q1;
            Q1=makeQuery(id+"F0.opExtrude","SWEPT_FACE",FACE,{"disambiguationData":[OSD([sQuery(id+"F3.wireOp",EDGE,"E98.0")])]});
            var Q2;
            Q2=makeQuery(id+"F0.opExtrude","SWEPT_FACE",FACE,{"disambiguationData":[OSD([sQuery(id+"F3.wireOp",EDGE,"E97.0")])]});
            var Q3;
            Q3=makeQuery(id+"F0.opExtrude","SWEPT_FACE",FACE,{"disambiguationData":[OSD([sQuery(id+"F3.wireOp",EDGE,"E100.0")])]});
            var Q4;
            Q4=makeQuery(id+"F0.opExtrude","SWEPT_FACE",FACE,{"disambiguationData":[OSD([sQuery(id+"F3.wireOp",EDGE,"E101.0")])]});
            var Q5;
            Q5=makeQuery(id+"F0.opExtrude","SWEPT_FACE",FACE,{"disambiguationData":[OSD([sQuery(id+"F3.wireOp",EDGE,"E96.0")])]});
            var Q6;
            Q6=makeQuery(id+"F0.opExtrude","SWEPT_FACE",FACE,{"disambiguationData":[OSD([sQuery(id+"F3.wireOp",EDGE,"E95.0")])]});
            var Q7;
            Q7=makeQuery(id+"F0.opExtrude","SWEPT_FACE",FACE,{"disambiguationData":[OSD([sQuery(id+"F3.wireOp",EDGE,"E93.0")])]});
            var Q8;
            Q8=makeQuery(id+"F0.opExtrude","SWEPT_FACE",FACE,{"disambiguationData":[OSD([sQuery(id+"F3.wireOp",EDGE,"E91.0")])]});
            var Q9;
            Q9=makeQuery(id+"F0.opExtrude","SWEPT_FACE",FACE,{"disambiguationData":[OSD([sQuery(id+"F3.wireOp",EDGE,"E89.0")])]});
            var Q10;
            Q10=makeQuery(id+"F0.opExtrude","SWEPT_FACE",FACE,{"disambiguationData":[OSD([sQuery(id+"F3.wireOp",EDGE,"E88.0")])]});
            var Q11;
            Q11=makeQuery(id+"F0.opExtrude","SWEPT_FACE",FACE,{"disambiguationData":[OSD([sQuery(id+"F3.wireOp",EDGE,"E87.0")])]});
            var Q12;
            Q12=makeQuery(id+"F0.opExtrude","SWEPT_FACE",FACE,{"disambiguationData":[OSD([sQuery(id+"F3.wireOp",EDGE,"E86.0")])]});
            var Q13;
            Q13=makeQuery(id+"F0.opExtrude","SWEPT_FACE",FACE,{"disambiguationData":[OSD([sQuery(id+"F3.wireOp",EDGE,"E85.0")])]});
            var Q14;
            Q14=makeQuery(id+"F0.opExtrude","SWEPT_FACE",FACE,{"disambiguationData":[OSD([sQuery(id+"F3.wireOp",EDGE,"E83.0")])]});
            var Q15;
            Q15=makeQuery(id+"F0.opExtrude","SWEPT_FACE",FACE,{"disambiguationData":[OSD([sQuery(id+"F3.wireOp",EDGE,"E82.0")])]});
            var Q16;
            Q16=makeQuery(id+"F0.opExtrude","SWEPT_FACE",FACE,{"disambiguationData":[OSD([sQuery(id+"F3.wireOp",EDGE,"E80.0")])]});
            var Q17;
            Q17=makeQuery(id+"F0.opExtrude","SWEPT_FACE",FACE,{"disambiguationData":[OSD([sQuery(id+"F3.wireOp",EDGE,"E79.0")])]});
            var Q18;
            Q18=makeQuery(id+"F0.opExtrude","SWEPT_FACE",FACE,{"disambiguationData":[OSD([sQuery(id+"F3.wireOp",EDGE,"E76.0")])]});
            var Q19;
            Q19=makeQuery(id+"F0.opExtrude","SWEPT_FACE",FACE,{"disambiguationData":[OSD([sQuery(id+"F3.wireOp",EDGE,"E74.0")])]});
            var Q20;
            Q20=makeQuery(id+"F0.opExtrude","SWEPT_FACE",FACE,{"disambiguationData":[OSD([sQuery(id+"F3.wireOp",EDGE,"E72.0")])]});
            var Q21;
            Q21=makeQuery(id+"F0.opExtrude","SWEPT_FACE",FACE,{"disambiguationData":[OSD([sQuery(id+"F3.wireOp",EDGE,"E70.0")])]});
            var Q22;
            Q22=makeQuery(id+"F0.opExtrude","SWEPT_FACE",FACE,{"disambiguationData":[OSD([sQuery(id+"F3.wireOp",EDGE,"E68.0")])]});
            var Q23;
            Q23=makeQuery(id+"F0.opExtrude","SWEPT_FACE",FACE,{"disambiguationData":[OSD([sQuery(id+"F3.wireOp",EDGE,"E64.0")])]});
            var Q24;
            Q24=makeQuery(id+"F0.opExtrude","SWEPT_FACE",FACE,{"disambiguationData":[OSD([sQuery(id+"F3.wireOp",EDGE,"E62.0")])]});
            var Q25;
            Q25=makeQuery(id+"F0.opExtrude","SWEPT_FACE",FACE,{"disambiguationData":[OSD([sQuery(id+"F3.wireOp",EDGE,"E66.0")])]});
            var Q26;
            Q26=makeQuery(id+"F0.opExtrude","SWEPT_FACE",FACE,{"disambiguationData":[OSD([sQuery(id+"F3.wireOp",EDGE,"E60.0")])]});
            fillet(context, id + "F2", {"entities" : qUnion([Q0, Q1, Q2, Q3, Q4, Q5, Q6, Q7, Q8, Q9, Q10, Q11, Q12, Q13, Q14, Q15, Q16, Q17, Q18, Q19, Q20, Q21, Q22, Q23, Q24, Q25, Q26]), "radius" : 1.78 * mm, "tangentPropagation" : true, "allowEdgeOverflow" : false});
        }
    });
